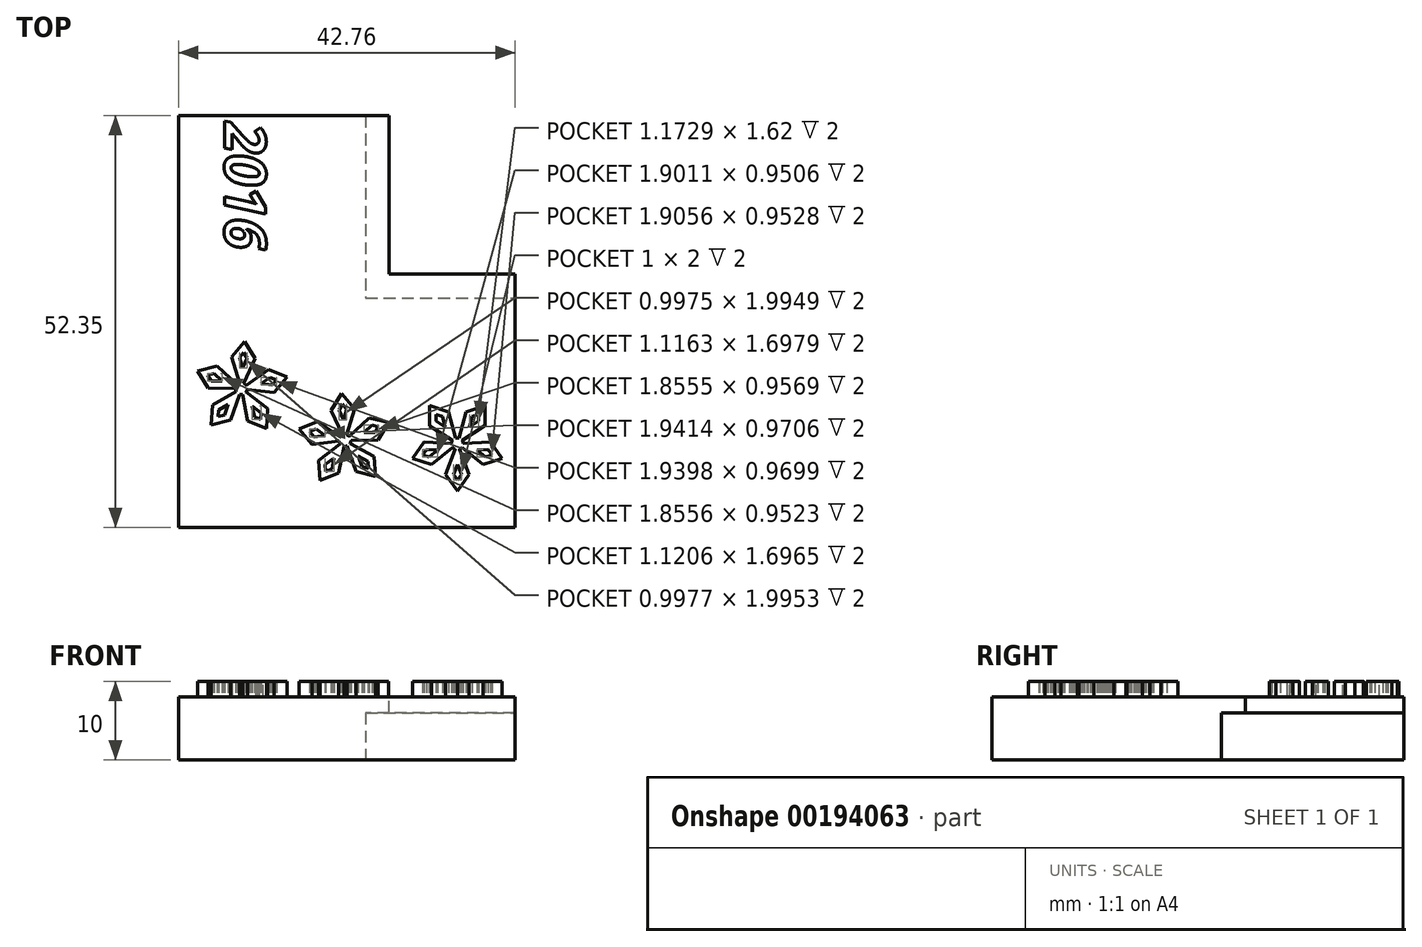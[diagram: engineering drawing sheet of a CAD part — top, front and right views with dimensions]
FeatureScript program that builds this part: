
annotation { "Feature Type Name" : "Feature", "Feature Type Description" : "" }
export const myFeature = defineFeature(function(context is Context, id is Id, definition is map)
    precondition{}
    {
        {
            var Q0;
            Q0=qCreatedBy(makeId("Top.planeOp"),FACE);
            var sketch = newSketch(context, id + "F0", { "sketchPlane" : qUnion([Q0])});
            skLineSegment(sketch, "E0.bottom", {"start": v(100, 80) * mm, "end": v(20, 80) * mm});
            skLineSegment(sketch, "E0.top", {"start": v(100, -80) * mm, "end": v(20, -80) * mm});
            skLineSegment(sketch, "E0.left", {"start": v(100, 80) * mm, "end": v(100, 20) * mm});
            skLineSegment(sketch, "E0.right", {"start": v(-100, 80) * mm, "end": v(-100, 20) * mm});
            skLineSegment(sketch, "E1.trimOffspring", {"start": v(-100, -20) * mm, "end": v(-100, -80) * mm});
            skLineSegment(sketch, "E2.trimOffspring", {"start": v(100, -20) * mm, "end": v(100, -80) * mm});
            skLineSegment(sketch, "E3.trimOffspring", {"start": v(-20, -80) * mm, "end": v(-100, -80) * mm});
            skLineSegment(sketch, "E4.trimOffspring", {"start": v(-20, 80) * mm, "end": v(-100, 80) * mm});
            skPoint(sketch, "E5.MirrorCS.end.orphan", {"position": v(100, 59.57) * mm});
            skPoint(sketch, "E5.MirrorCS.start.orphan", {"position": v(125, 0) * mm});
            skPoint(sketch, "E6.orphan", {"position": v(100, -59.57) * mm});
            skLineSegment(sketch, "E7", {"start": v(20, 80) * mm, "end": v(-20, 80) * mm});
            skLineSegment(sketch, "E8", {"start": v(100, 20) * mm, "end": v(100, -20) * mm});
            skLineSegment(sketch, "E9", {"start": v(20, -80) * mm, "end": v(-20, -80) * mm});
            skLineSegment(sketch, "E10", {"start": v(-100, -20) * mm, "end": v(-100, 20) * mm});
            skPoint(sketch, "E11.MirrorCS.end.orphan", {"position": v(0, -105) * mm});
            skPoint(sketch, "E12.start.orphan", {"position": v(0, 105) * mm});
            skPoint(sketch, "E13.MirrorCS.end.orphan", {"position": v(-125, 0) * mm});
            skSolve(sketch);
        }
        {
            var Q0;
            Q0=qSketchRegion(id+"F0",true);
            extrude(context, id + "F1", {"entities" : qUnion([Q0]), "endBound" : BoundingType.SYMMETRIC, "depth" : 8 * mm});
        }
        {
            var Q0;
            Q0=makeQuery(id+"F1.opExtrude","CAP_FACE",FACE,{"disambiguationData":[OSD([sQuery(id+"F0.wireOp",EDGE,"E0.bottom"),sQuery(id+"F0.wireOp",EDGE,"E0.top"),sQuery(id+"F0.wireOp",EDGE,"E0.left"),sQuery(id+"F0.wireOp",EDGE,"E0.right"),sQuery(id+"F0.wireOp",EDGE,"b7ca5f3b-2874-41bd-b902-1c79f96a0a8620.MirrorC"),sQuery(id+"F0.wireOp",EDGE,"b7ca5f3b-2874-41bd-b902-1c79f96a0a8621.MirrorC"),sQuery(id+"F0.wireOp",EDGE,"b7ca5f3b-2874-41bd-b902-1c79f96a0a8622.MirrorCS"),sQuery(id+"F0.wireOp",EDGE,"b7ca5f3b-2874-41bd-b902-1c79f96a0a8623.MirrorCS"),sQuery(id+"F0.wireOp",EDGE,"b7ca5f3b-2874-41bd-b902-1c79f96a0a8624.MirrorCS"),sQuery(id+"F0.wireOp",EDGE,"b7ca5f3b-2874-41bd-b902-1c79f96a0a8625.MirrorCS"),sQuery(id+"F0.wireOp",EDGE,"70034771-ba44-435e-ab74-29499f25fa1546.MirrorC"),sQuery(id+"F0.wireOp",EDGE,"70034771-ba44-435e-ab74-29499f25fa1547.MirrorCS"),sQuery(id+"F0.wireOp",EDGE,"70034771-ba44-435e-ab74-29499f25fa1548.MirrorC"),sQuery(id+"F0.wireOp",EDGE,"70034771-ba44-435e-ab74-29499f25fa1549.MirrorCS"),sQuery(id+"F0.wireOp",EDGE,"70034771-ba44-435e-ab74-29499f25fa1550.MirrorCS"),sQuery(id+"F0.wireOp",EDGE,"70034771-ba44-435e-ab74-29499f25fa1551.MirrorCS"),sQuery(id+"F0.wireOp",EDGE,"kvcqsOdL-v7G7-uprB-0sNa-MCxYedLtEpX4"),sQuery(id+"F0.wireOp",EDGE,"FiKvVNeF-WQ3T-xo78-YCTY-fOMMCtKvFc36"),sQuery(id+"F0.wireOp",EDGE,"E12"),sQuery(id+"F0.wireOp",EDGE,"E11.MirrorCS"),sQuery(id+"F0.wireOp",EDGE,"c8cf1958-df2a-43db-8a51-ccb89cce498c1.MirrorCS"),sQuery(id+"F0.wireOp",EDGE,"b5f25a3e-5a5b-413b-84b4-cc5ad052e2f90.MirrorCS"),sQuery(id+"F0.wireOp",EDGE,"E13.MirrorCS"),sQuery(id+"F0.wireOp",EDGE,"bd7b76a7-2dc2-4ffb-bbfe-847ced00b9070.MirrorCS"),sQuery(id+"F0.wireOp",EDGE,"E1.trimOffspring"),sQuery(id+"F0.wireOp",EDGE,"E2.trimOffspring"),sQuery(id+"F0.wireOp",EDGE,"E3.trimOffspring"),sQuery(id+"F0.wireOp",EDGE,"E4.trimOffspring")])],"isStart":false});
            var sketch = newSketch(context, id + "F2", { "sketchPlane" : qUnion([Q0])});
            skCircle(sketch, "E14.cCircle", {"center": v(82.22, 58.96) * mm, "radius": 6 * mm, "construction": true});
            skLineSegment(sketch, "E14.0", {"start": v(88.2, 58.66) * mm, "end": v(83.78, 53.17) * mm, "construction": true});
            skLineSegment(sketch, "E14.1", {"start": v(83.78, 53.17) * mm, "end": v(77.19, 55.68) * mm, "construction": true});
            skLineSegment(sketch, "E14.2", {"start": v(77.19, 55.68) * mm, "end": v(77.55, 62.73) * mm, "construction": true});
            skLineSegment(sketch, "E14.3", {"start": v(63.31, 55.4) * mm, "end": v(70.12, 57.24) * mm, "construction": true});
            skLineSegment(sketch, "E14.4", {"start": v(84.36, 64.57) * mm, "end": v(88.2, 58.66) * mm, "construction": true});
            skLineSegment(sketch, "E15", {"start": v(77.55, 62.73) * mm, "end": v(78.22, 60.26) * mm});
            skLineSegment(sketch, "E16", {"start": v(78.22, 60.26) * mm, "end": v(81.5, 59.2) * mm});
            skLineSegment(sketch, "E17", {"start": v(81.84, 59.6) * mm, "end": v(80.1, 62.6) * mm});
            skLineSegment(sketch, "E18", {"start": v(80.1, 62.6) * mm, "end": v(77.55, 62.73) * mm});
            skLineSegment(sketch, "E19", {"start": v(77.19, 55.68) * mm, "end": v(79.74, 55.56) * mm});
            skLineSegment(sketch, "E20", {"start": v(79.74, 55.56) * mm, "end": v(81.77, 58.35) * mm});
            skLineSegment(sketch, "E21", {"start": v(81.48, 58.8) * mm, "end": v(78.1, 58.07) * mm});
            skLineSegment(sketch, "E22", {"start": v(78.1, 58.07) * mm, "end": v(77.19, 55.68) * mm});
            skLineSegment(sketch, "E23", {"start": v(83.78, 53.17) * mm, "end": v(84.69, 55.56) * mm});
            skLineSegment(sketch, "E24", {"start": v(84.69, 55.56) * mm, "end": v(82.66, 58.35) * mm});
            skLineSegment(sketch, "E25", {"start": v(82.14, 58.21) * mm, "end": v(81.8, 54.78) * mm});
            skLineSegment(sketch, "E26", {"start": v(81.8, 54.78) * mm, "end": v(83.78, 53.17) * mm});
            skLineSegment(sketch, "E27", {"start": v(82.9, 58.66) * mm, "end": v(86.06, 57.26) * mm});
            skLineSegment(sketch, "E28", {"start": v(86.06, 57.26) * mm, "end": v(88.2, 58.66) * mm});
            skLineSegment(sketch, "E29", {"start": v(82.93, 59.2) * mm, "end": v(86.21, 60.26) * mm});
            skLineSegment(sketch, "E30", {"start": v(86.21, 60.26) * mm, "end": v(88.2, 58.66) * mm});
            skLineSegment(sketch, "E31", {"start": v(84.36, 64.57) * mm, "end": v(85.02, 62.1) * mm});
            skLineSegment(sketch, "E32", {"start": v(85.02, 62.1) * mm, "end": v(82.72, 59.52) * mm});
            skLineSegment(sketch, "E33", {"start": v(82.22, 59.71) * mm, "end": v(82.22, 63.16) * mm});
            skLineSegment(sketch, "E34", {"start": v(82.22, 63.16) * mm, "end": v(84.36, 64.57) * mm});
            skLineSegment(sketch, "E35", {"start": v(86.28, 61.61) * mm, "end": v(86, 55.91) * mm, "construction": true});
            skLineSegment(sketch, "E36", {"start": v(86, 55.91) * mm, "end": v(80.48, 54.43) * mm, "construction": true});
            skLineSegment(sketch, "E37", {"start": v(80.48, 54.43) * mm, "end": v(77.37, 59.2) * mm, "construction": true});
            skLineSegment(sketch, "E38", {"start": v(77.37, 59.2) * mm, "end": v(80.95, 63.65) * mm, "construction": true});
            skLineSegment(sketch, "E39", {"start": v(80.95, 63.65) * mm, "end": v(86.28, 61.61) * mm, "construction": true});
            skLineSegment(sketch, "E40", {"start": v(84.36, 64.57) * mm, "end": v(82.22, 58.96) * mm, "construction": true});
            skLineSegment(sketch, "E41", {"start": v(88.2, 58.66) * mm, "end": v(82.22, 58.96) * mm, "construction": true});
            skLineSegment(sketch, "E42", {"start": v(83.78, 53.17) * mm, "end": v(82.22, 58.96) * mm, "construction": true});
            skLineSegment(sketch, "E43", {"start": v(77.19, 55.68) * mm, "end": v(82.22, 58.96) * mm, "construction": true});
            skLineSegment(sketch, "E44", {"start": v(77.55, 62.73) * mm, "end": v(82.22, 58.96) * mm, "construction": true});
            skArc(sketch, "E45", {"start": v(81.77, 58.35) * mm, "mid": v(81.95, 58.26) * mm, "end": v(82.14, 58.21) * mm});
            skArc(sketch, "E46.trimOffspring", {"start": v(81.5, 59.2) * mm, "mid": v(81.47, 59) * mm, "end": v(81.48, 58.8) * mm});
            skArc(sketch, "E47.trimOffspring", {"start": v(82.22, 59.71) * mm, "mid": v(82.02, 59.69) * mm, "end": v(81.84, 59.6) * mm});
            skArc(sketch, "E48.trimOffspring", {"start": v(82.93, 59.2) * mm, "mid": v(82.84, 59.37) * mm, "end": v(82.72, 59.52) * mm});
            skArc(sketch, "E49.trimOffspring", {"start": v(82.66, 58.35) * mm, "mid": v(82.8, 58.49) * mm, "end": v(82.9, 58.66) * mm});
            skLineSegment(sketch, "E50", {"start": v(78.62, 61.86) * mm, "end": v(78.85, 61.04) * mm});
            skLineSegment(sketch, "E51", {"start": v(78.85, 61.04) * mm, "end": v(80.18, 60.6) * mm});
            skLineSegment(sketch, "E52", {"start": v(80.18, 60.6) * mm, "end": v(79.47, 61.82) * mm});
            skLineSegment(sketch, "E53", {"start": v(79.47, 61.82) * mm, "end": v(78.62, 61.86) * mm});
            skLineSegment(sketch, "E54", {"start": v(83.86, 63.28) * mm, "end": v(84.08, 62.45) * mm});
            skLineSegment(sketch, "E55", {"start": v(84.08, 62.45) * mm, "end": v(83.15, 61.4) * mm});
            skLineSegment(sketch, "E56", {"start": v(83.15, 61.4) * mm, "end": v(83.15, 62.8) * mm});
            skLineSegment(sketch, "E57", {"start": v(83.15, 62.8) * mm, "end": v(83.86, 63.28) * mm});
            skLineSegment(sketch, "E58", {"start": v(83.42, 54.5) * mm, "end": v(83.72, 55.3) * mm});
            skLineSegment(sketch, "E59", {"start": v(83.72, 55.3) * mm, "end": v(82.9, 56.43) * mm});
            skLineSegment(sketch, "E60", {"start": v(82.9, 56.43) * mm, "end": v(82.76, 55.04) * mm});
            skLineSegment(sketch, "E61", {"start": v(82.76, 55.04) * mm, "end": v(83.42, 54.5) * mm});
            skLineSegment(sketch, "E62", {"start": v(86.83, 58.73) * mm, "end": v(86.16, 59.26) * mm});
            skLineSegment(sketch, "E63", {"start": v(86.16, 59.26) * mm, "end": v(84.83, 58.83) * mm});
            skLineSegment(sketch, "E64", {"start": v(84.83, 58.83) * mm, "end": v(86.11, 58.26) * mm});
            skLineSegment(sketch, "E65", {"start": v(86.11, 58.26) * mm, "end": v(86.83, 58.73) * mm});
            skLineSegment(sketch, "E66", {"start": v(78.35, 56.44) * mm, "end": v(79.2, 56.4) * mm});
            skLineSegment(sketch, "E67", {"start": v(79.2, 56.4) * mm, "end": v(80.02, 57.53) * mm});
            skLineSegment(sketch, "E68", {"start": v(80.02, 57.53) * mm, "end": v(78.65, 57.24) * mm});
            skLineSegment(sketch, "E69", {"start": v(78.65, 57.24) * mm, "end": v(78.35, 56.44) * mm});
            skLineSegment(sketch, "E70", {"start": v(78.1, 29.78) * mm, "end": v(78.11, 27.22) * mm});
            skLineSegment(sketch, "E71", {"start": v(78.11, 27.22) * mm, "end": v(81, 25.34) * mm});
            skLineSegment(sketch, "E72", {"start": v(81.44, 25.66) * mm, "end": v(80.54, 29) * mm});
            skLineSegment(sketch, "E73", {"start": v(80.54, 29) * mm, "end": v(78.1, 29.78) * mm});
            skLineSegment(sketch, "E74", {"start": v(75.93, 23.07) * mm, "end": v(78.37, 22.29) * mm});
            skLineSegment(sketch, "E75", {"start": v(78.37, 22.29) * mm, "end": v(81.05, 24.46) * mm});
            skLineSegment(sketch, "E76", {"start": v(80.89, 24.97) * mm, "end": v(77.44, 25.14) * mm});
            skLineSegment(sketch, "E77", {"start": v(77.44, 25.14) * mm, "end": v(75.93, 23.07) * mm});
            skLineSegment(sketch, "E78", {"start": v(81.65, 18.93) * mm, "end": v(83.14, 21) * mm});
            skLineSegment(sketch, "E79", {"start": v(83.14, 21) * mm, "end": v(81.9, 24.23) * mm});
            skLineSegment(sketch, "E80", {"start": v(81.37, 24.23) * mm, "end": v(80.14, 21) * mm});
            skLineSegment(sketch, "E81", {"start": v(80.14, 21) * mm, "end": v(81.65, 18.93) * mm});
            skLineSegment(sketch, "E82", {"start": v(82.22, 24.46) * mm, "end": v(84.91, 22.3) * mm});
            skLineSegment(sketch, "E83", {"start": v(84.91, 22.3) * mm, "end": v(87.35, 23.09) * mm});
            skLineSegment(sketch, "E84", {"start": v(82.39, 24.97) * mm, "end": v(85.83, 25.15) * mm});
            skLineSegment(sketch, "E85", {"start": v(85.83, 25.15) * mm, "end": v(87.35, 23.09) * mm});
            skLineSegment(sketch, "E86", {"start": v(85.16, 29.8) * mm, "end": v(85.15, 27.24) * mm});
            skLineSegment(sketch, "E87", {"start": v(85.15, 27.24) * mm, "end": v(82.26, 25.34) * mm});
            skLineSegment(sketch, "E88", {"start": v(81.83, 25.66) * mm, "end": v(82.72, 29) * mm});
            skLineSegment(sketch, "E89", {"start": v(82.72, 29) * mm, "end": v(85.16, 29.8) * mm});
            skArc(sketch, "E90", {"start": v(81.05, 24.46) * mm, "mid": v(81.2, 24.33) * mm, "end": v(81.37, 24.23) * mm});
            skArc(sketch, "E91.trimOffspring", {"start": v(81, 25.34) * mm, "mid": v(80.92, 25.17) * mm, "end": v(80.89, 24.97) * mm});
            skArc(sketch, "E92.trimOffspring", {"start": v(81.83, 25.66) * mm, "mid": v(81.64, 25.68) * mm, "end": v(81.44, 25.66) * mm});
            skArc(sketch, "E93.trimOffspring", {"start": v(82.39, 24.97) * mm, "mid": v(82.35, 25.17) * mm, "end": v(82.26, 25.34) * mm});
            skArc(sketch, "E94.trimOffspring", {"start": v(81.9, 24.23) * mm, "mid": v(82.08, 24.33) * mm, "end": v(82.22, 24.46) * mm});
            skLineSegment(sketch, "E95", {"start": v(78.92, 28.67) * mm, "end": v(78.92, 27.81) * mm});
            skLineSegment(sketch, "E96", {"start": v(78.92, 27.81) * mm, "end": v(80.1, 27.05) * mm});
            skLineSegment(sketch, "E97", {"start": v(80.1, 27.05) * mm, "end": v(79.73, 28.4) * mm});
            skLineSegment(sketch, "E98", {"start": v(79.73, 28.4) * mm, "end": v(78.92, 28.67) * mm});
            skLineSegment(sketch, "E99", {"start": v(84.34, 28.67) * mm, "end": v(84.34, 27.82) * mm});
            skLineSegment(sketch, "E100", {"start": v(84.34, 27.82) * mm, "end": v(83.17, 27.06) * mm});
            skLineSegment(sketch, "E101", {"start": v(83.17, 27.06) * mm, "end": v(83.53, 28.4) * mm});
            skLineSegment(sketch, "E102", {"start": v(83.53, 28.4) * mm, "end": v(84.34, 28.67) * mm});
            skLineSegment(sketch, "E103", {"start": v(81.64, 20.32) * mm, "end": v(82.14, 21) * mm});
            skLineSegment(sketch, "E104", {"start": v(82.14, 21) * mm, "end": v(81.64, 22.32) * mm});
            skLineSegment(sketch, "E105", {"start": v(81.64, 22.32) * mm, "end": v(81.14, 21) * mm});
            skLineSegment(sketch, "E106", {"start": v(81.14, 21) * mm, "end": v(81.64, 20.32) * mm});
            skLineSegment(sketch, "E107", {"start": v(86.03, 23.51) * mm, "end": v(85.53, 24.2) * mm});
            skLineSegment(sketch, "E108", {"start": v(85.53, 24.2) * mm, "end": v(84.13, 24.13) * mm});
            skLineSegment(sketch, "E109", {"start": v(84.13, 24.13) * mm, "end": v(85.22, 23.25) * mm});
            skLineSegment(sketch, "E110", {"start": v(85.22, 23.25) * mm, "end": v(86.03, 23.51) * mm});
            skLineSegment(sketch, "E111", {"start": v(77.25, 23.5) * mm, "end": v(78.06, 23.24) * mm});
            skLineSegment(sketch, "E112", {"start": v(78.06, 23.24) * mm, "end": v(79.15, 24.12) * mm});
            skLineSegment(sketch, "E113", {"start": v(79.15, 24.12) * mm, "end": v(77.75, 24.19) * mm});
            skLineSegment(sketch, "E114", {"start": v(77.75, 24.19) * mm, "end": v(77.25, 23.5) * mm});
            skLineSegment(sketch, "E115", {"start": v(54.66, 73.05) * mm, "end": v(55.75, 70.73) * mm});
            skLineSegment(sketch, "E116", {"start": v(55.75, 70.73) * mm, "end": v(59.17, 70.25) * mm});
            skLineSegment(sketch, "E117", {"start": v(59.43, 70.72) * mm, "end": v(57.2, 73.36) * mm});
            skLineSegment(sketch, "E118", {"start": v(57.2, 73.36) * mm, "end": v(54.66, 73.05) * mm});
            skLineSegment(sketch, "E119", {"start": v(55.53, 66.05) * mm, "end": v(58.07, 66.37) * mm});
            skLineSegment(sketch, "E120", {"start": v(58.07, 66.37) * mm, "end": v(59.58, 69.47) * mm});
            skLineSegment(sketch, "E121", {"start": v(59.22, 69.86) * mm, "end": v(56.02, 68.56) * mm});
            skLineSegment(sketch, "E122", {"start": v(56.02, 68.56) * mm, "end": v(55.53, 66.05) * mm});
            skLineSegment(sketch, "E123", {"start": v(62.46, 64.71) * mm, "end": v(62.94, 67.23) * mm});
            skLineSegment(sketch, "E124", {"start": v(62.94, 67.23) * mm, "end": v(60.45, 69.63) * mm});
            skLineSegment(sketch, "E125", {"start": v(59.97, 69.4) * mm, "end": v(60.22, 65.95) * mm});
            skLineSegment(sketch, "E126", {"start": v(60.22, 65.95) * mm, "end": v(62.46, 64.71) * mm});
            skLineSegment(sketch, "E127", {"start": v(60.64, 69.97) * mm, "end": v(64, 69.14) * mm});
            skLineSegment(sketch, "E128", {"start": v(64, 69.14) * mm, "end": v(65.87, 70.89) * mm});
            skLineSegment(sketch, "E129", {"start": v(60.58, 70.5) * mm, "end": v(63.62, 72.12) * mm});
            skLineSegment(sketch, "E130", {"start": v(63.62, 72.12) * mm, "end": v(65.87, 70.89) * mm});
            skLineSegment(sketch, "E131", {"start": v(61.05, 76.04) * mm, "end": v(62.13, 73.72) * mm});
            skLineSegment(sketch, "E132", {"start": v(62.13, 73.72) * mm, "end": v(60.3, 70.78) * mm});
            skLineSegment(sketch, "E133", {"start": v(59.78, 70.89) * mm, "end": v(59.18, 74.29) * mm});
            skLineSegment(sketch, "E134", {"start": v(59.18, 74.29) * mm, "end": v(61.05, 76.04) * mm});
            skArc(sketch, "E135", {"start": v(59.58, 69.47) * mm, "mid": v(59.77, 69.41) * mm, "end": v(59.97, 69.4) * mm});
            skArc(sketch, "E136.trimOffspring", {"start": v(59.17, 70.25) * mm, "mid": v(59.17, 70.05) * mm, "end": v(59.22, 69.86) * mm});
            skArc(sketch, "E137.trimOffspring", {"start": v(59.78, 70.89) * mm, "mid": v(59.6, 70.83) * mm, "end": v(59.43, 70.72) * mm});
            skArc(sketch, "E138.trimOffspring", {"start": v(60.58, 70.5) * mm, "mid": v(60.46, 70.66) * mm, "end": v(60.3, 70.78) * mm});
            skArc(sketch, "E139.trimOffspring", {"start": v(60.45, 69.63) * mm, "mid": v(60.57, 69.78) * mm, "end": v(60.64, 69.97) * mm});
            skLineSegment(sketch, "E140", {"start": v(55.87, 72.38) * mm, "end": v(56.23, 71.6) * mm});
            skLineSegment(sketch, "E141", {"start": v(56.23, 71.6) * mm, "end": v(57.62, 71.41) * mm});
            skLineSegment(sketch, "E142", {"start": v(57.62, 71.41) * mm, "end": v(56.72, 72.48) * mm});
            skLineSegment(sketch, "E143", {"start": v(56.72, 72.48) * mm, "end": v(55.87, 72.38) * mm});
            skLineSegment(sketch, "E144", {"start": v(60.79, 74.68) * mm, "end": v(61.15, 73.9) * mm});
            skLineSegment(sketch, "E145", {"start": v(61.15, 73.9) * mm, "end": v(60.4, 72.72) * mm});
            skLineSegment(sketch, "E146", {"start": v(60.4, 72.72) * mm, "end": v(60.17, 74.1) * mm});
            skLineSegment(sketch, "E147", {"start": v(60.17, 74.1) * mm, "end": v(60.79, 74.68) * mm});
            skLineSegment(sketch, "E148", {"start": v(61.87, 65.96) * mm, "end": v(62.03, 66.8) * mm});
            skLineSegment(sketch, "E149", {"start": v(62.03, 66.8) * mm, "end": v(61.02, 67.78) * mm});
            skLineSegment(sketch, "E150", {"start": v(61.02, 67.78) * mm, "end": v(61.13, 66.38) * mm});
            skLineSegment(sketch, "E151", {"start": v(61.13, 66.38) * mm, "end": v(61.87, 65.96) * mm});
            skLineSegment(sketch, "E152", {"start": v(64.5, 70.72) * mm, "end": v(63.75, 71.13) * mm});
            skLineSegment(sketch, "E153", {"start": v(63.75, 71.13) * mm, "end": v(62.5, 70.47) * mm});
            skLineSegment(sketch, "E154", {"start": v(62.5, 70.47) * mm, "end": v(63.87, 70.13) * mm});
            skLineSegment(sketch, "E155", {"start": v(63.87, 70.13) * mm, "end": v(64.5, 70.72) * mm});
            skLineSegment(sketch, "E156", {"start": v(56.54, 67) * mm, "end": v(57.39, 67.1) * mm});
            skLineSegment(sketch, "E157", {"start": v(57.39, 67.1) * mm, "end": v(58, 68.36) * mm});
            skLineSegment(sketch, "E158", {"start": v(58, 68.36) * mm, "end": v(56.7, 67.83) * mm});
            skLineSegment(sketch, "E159", {"start": v(56.7, 67.83) * mm, "end": v(56.54, 67) * mm});
            skLineSegment(sketch, "E160", {"start": v(86.68, 11.24) * mm, "end": v(87.35, 8.78) * mm});
            skLineSegment(sketch, "E161", {"start": v(87.35, 8.78) * mm, "end": v(90.64, 7.7) * mm});
            skLineSegment(sketch, "E162", {"start": v(90.97, 8.12) * mm, "end": v(89.24, 11.1) * mm});
            skLineSegment(sketch, "E163", {"start": v(89.24, 11.1) * mm, "end": v(86.68, 11.24) * mm});
            skLineSegment(sketch, "E164", {"start": v(86.32, 4.2) * mm, "end": v(88.88, 4.08) * mm});
            skLineSegment(sketch, "E165", {"start": v(88.88, 4.08) * mm, "end": v(90.91, 6.87) * mm});
            skLineSegment(sketch, "E166", {"start": v(90.62, 7.32) * mm, "end": v(87.24, 6.59) * mm});
            skLineSegment(sketch, "E167", {"start": v(87.24, 6.59) * mm, "end": v(86.32, 4.2) * mm});
            skLineSegment(sketch, "E168", {"start": v(92.91, 1.68) * mm, "end": v(93.82, 4.08) * mm});
            skLineSegment(sketch, "E169", {"start": v(93.82, 4.08) * mm, "end": v(91.8, 6.87) * mm});
            skLineSegment(sketch, "E170", {"start": v(91.27, 6.73) * mm, "end": v(90.93, 3.3) * mm});
            skLineSegment(sketch, "E171", {"start": v(90.93, 3.3) * mm, "end": v(92.91, 1.68) * mm});
            skLineSegment(sketch, "E172", {"start": v(92.04, 7.17) * mm, "end": v(95.2, 5.78) * mm});
            skLineSegment(sketch, "E173", {"start": v(95.2, 5.78) * mm, "end": v(97.34, 7.17) * mm});
            skLineSegment(sketch, "E174", {"start": v(92.06, 7.7) * mm, "end": v(95.35, 8.78) * mm});
            skLineSegment(sketch, "E175", {"start": v(95.35, 8.78) * mm, "end": v(97.34, 7.17) * mm});
            skLineSegment(sketch, "E176", {"start": v(93.5, 13.08) * mm, "end": v(94.15, 10.6) * mm});
            skLineSegment(sketch, "E177", {"start": v(94.15, 10.6) * mm, "end": v(91.85, 8.04) * mm});
            skLineSegment(sketch, "E178", {"start": v(91.35, 8.23) * mm, "end": v(91.35, 11.68) * mm});
            skLineSegment(sketch, "E179", {"start": v(91.35, 11.68) * mm, "end": v(93.5, 13.08) * mm});
            skArc(sketch, "E180", {"start": v(90.91, 6.87) * mm, "mid": v(91.08, 6.78) * mm, "end": v(91.27, 6.73) * mm});
            skArc(sketch, "E181.trimOffspring", {"start": v(90.64, 7.7) * mm, "mid": v(90.6, 7.51) * mm, "end": v(90.62, 7.32) * mm});
            skArc(sketch, "E182.trimOffspring", {"start": v(91.35, 8.23) * mm, "mid": v(91.16, 8.2) * mm, "end": v(90.97, 8.12) * mm});
            skArc(sketch, "E183.trimOffspring", {"start": v(92.06, 7.7) * mm, "mid": v(91.98, 7.89) * mm, "end": v(91.85, 8.04) * mm});
            skArc(sketch, "E184.trimOffspring", {"start": v(91.8, 6.87) * mm, "mid": v(91.93, 7) * mm, "end": v(92.04, 7.17) * mm});
            skLineSegment(sketch, "E185", {"start": v(87.76, 10.38) * mm, "end": v(87.98, 9.55) * mm});
            skLineSegment(sketch, "E186", {"start": v(87.98, 9.55) * mm, "end": v(89.31, 9.12) * mm});
            skLineSegment(sketch, "E187", {"start": v(89.31, 9.12) * mm, "end": v(88.6, 10.33) * mm});
            skLineSegment(sketch, "E188", {"start": v(88.6, 10.33) * mm, "end": v(87.76, 10.38) * mm});
            skLineSegment(sketch, "E189", {"start": v(93, 11.8) * mm, "end": v(93.22, 10.97) * mm});
            skLineSegment(sketch, "E190", {"start": v(93.22, 10.97) * mm, "end": v(92.29, 9.92) * mm});
            skLineSegment(sketch, "E191", {"start": v(92.29, 9.92) * mm, "end": v(92.29, 11.32) * mm});
            skLineSegment(sketch, "E192", {"start": v(92.29, 11.32) * mm, "end": v(93, 11.8) * mm});
            skLineSegment(sketch, "E193", {"start": v(92.55, 3.02) * mm, "end": v(92.86, 3.81) * mm});
            skLineSegment(sketch, "E194", {"start": v(92.86, 3.81) * mm, "end": v(92.03, 4.95) * mm});
            skLineSegment(sketch, "E195", {"start": v(92.03, 4.95) * mm, "end": v(91.9, 3.55) * mm});
            skLineSegment(sketch, "E196", {"start": v(91.9, 3.55) * mm, "end": v(92.55, 3.02) * mm});
            skLineSegment(sketch, "E197", {"start": v(95.96, 7.24) * mm, "end": v(95.3, 7.78) * mm});
            skLineSegment(sketch, "E198", {"start": v(95.3, 7.78) * mm, "end": v(93.96, 7.34) * mm});
            skLineSegment(sketch, "E199", {"start": v(93.96, 7.34) * mm, "end": v(95.25, 6.78) * mm});
            skLineSegment(sketch, "E200", {"start": v(95.25, 6.78) * mm, "end": v(95.96, 7.24) * mm});
            skLineSegment(sketch, "E201", {"start": v(87.48, 4.95) * mm, "end": v(88.33, 4.91) * mm});
            skLineSegment(sketch, "E202", {"start": v(88.33, 4.91) * mm, "end": v(89.16, 6.05) * mm});
            skLineSegment(sketch, "E203", {"start": v(89.16, 6.05) * mm, "end": v(87.79, 5.75) * mm});
            skLineSegment(sketch, "E204", {"start": v(87.79, 5.75) * mm, "end": v(87.48, 4.95) * mm});
            skLineSegment(sketch, "E205", {"start": v(76.28, -11.06) * mm, "end": v(77.37, -13.38) * mm});
            skLineSegment(sketch, "E206", {"start": v(77.37, -13.38) * mm, "end": v(80.8, -13.86) * mm});
            skLineSegment(sketch, "E207", {"start": v(81.05, -13.4) * mm, "end": v(78.82, -10.75) * mm});
            skLineSegment(sketch, "E208", {"start": v(78.82, -10.75) * mm, "end": v(76.28, -11.06) * mm});
            skLineSegment(sketch, "E209", {"start": v(77.15, -18.06) * mm, "end": v(79.7, -17.74) * mm});
            skLineSegment(sketch, "E210", {"start": v(79.7, -17.74) * mm, "end": v(81.2, -14.64) * mm});
            skLineSegment(sketch, "E211", {"start": v(80.84, -14.25) * mm, "end": v(77.64, -15.55) * mm});
            skLineSegment(sketch, "E212", {"start": v(77.64, -15.55) * mm, "end": v(77.15, -18.06) * mm});
            skLineSegment(sketch, "E213", {"start": v(84.08, -19.4) * mm, "end": v(84.56, -16.88) * mm});
            skLineSegment(sketch, "E214", {"start": v(84.56, -16.88) * mm, "end": v(82.08, -14.49) * mm});
            skLineSegment(sketch, "E215", {"start": v(81.6, -14.71) * mm, "end": v(81.84, -18.16) * mm});
            skLineSegment(sketch, "E216", {"start": v(81.84, -18.16) * mm, "end": v(84.08, -19.4) * mm});
            skLineSegment(sketch, "E217", {"start": v(82.26, -14.14) * mm, "end": v(85.62, -14.97) * mm});
            skLineSegment(sketch, "E218", {"start": v(85.62, -14.97) * mm, "end": v(87.49, -13.22) * mm});
            skLineSegment(sketch, "E219", {"start": v(82.2, -13.61) * mm, "end": v(85.25, -12) * mm});
            skLineSegment(sketch, "E220", {"start": v(85.25, -12) * mm, "end": v(87.49, -13.22) * mm});
            skLineSegment(sketch, "E221", {"start": v(82.67, -8.07) * mm, "end": v(83.75, -10.4) * mm});
            skLineSegment(sketch, "E222", {"start": v(83.75, -10.4) * mm, "end": v(81.93, -13.33) * mm});
            skLineSegment(sketch, "E223", {"start": v(81.4, -13.23) * mm, "end": v(80.8, -9.82) * mm});
            skLineSegment(sketch, "E224", {"start": v(80.8, -9.82) * mm, "end": v(82.67, -8.07) * mm});
            skArc(sketch, "E225", {"start": v(81.2, -14.64) * mm, "mid": v(81.4, -14.7) * mm, "end": v(81.6, -14.71) * mm});
            skArc(sketch, "E226.trimOffspring", {"start": v(80.8, -13.86) * mm, "mid": v(80.8, -14.06) * mm, "end": v(80.84, -14.25) * mm});
            skArc(sketch, "E227.trimOffspring", {"start": v(81.4, -13.23) * mm, "mid": v(81.22, -13.29) * mm, "end": v(81.05, -13.4) * mm});
            skArc(sketch, "E228.trimOffspring", {"start": v(82.2, -13.61) * mm, "mid": v(82.08, -13.45) * mm, "end": v(81.93, -13.33) * mm});
            skArc(sketch, "E229.trimOffspring", {"start": v(82.08, -14.49) * mm, "mid": v(82.2, -14.33) * mm, "end": v(82.26, -14.14) * mm});
            skLineSegment(sketch, "E230", {"start": v(77.5, -11.73) * mm, "end": v(77.86, -12.5) * mm});
            skLineSegment(sketch, "E231", {"start": v(77.86, -12.5) * mm, "end": v(79.24, -12.7) * mm});
            skLineSegment(sketch, "E232", {"start": v(79.24, -12.7) * mm, "end": v(78.34, -11.63) * mm});
            skLineSegment(sketch, "E233", {"start": v(78.34, -11.63) * mm, "end": v(77.5, -11.73) * mm});
            skLineSegment(sketch, "E234", {"start": v(82.4, -9.43) * mm, "end": v(82.77, -10.2) * mm});
            skLineSegment(sketch, "E235", {"start": v(82.77, -10.2) * mm, "end": v(82.03, -11.4) * mm});
            skLineSegment(sketch, "E236", {"start": v(82.03, -11.4) * mm, "end": v(81.79, -10.01) * mm});
            skLineSegment(sketch, "E237", {"start": v(81.79, -10.01) * mm, "end": v(82.4, -9.43) * mm});
            skLineSegment(sketch, "E238", {"start": v(83.5, -18.15) * mm, "end": v(83.65, -17.3) * mm});
            skLineSegment(sketch, "E239", {"start": v(83.65, -17.3) * mm, "end": v(82.65, -16.34) * mm});
            skLineSegment(sketch, "E240", {"start": v(82.65, -16.34) * mm, "end": v(82.75, -17.73) * mm});
            skLineSegment(sketch, "E241", {"start": v(82.75, -17.73) * mm, "end": v(83.5, -18.15) * mm});
            skLineSegment(sketch, "E242", {"start": v(86.12, -13.4) * mm, "end": v(85.37, -12.98) * mm});
            skLineSegment(sketch, "E243", {"start": v(85.37, -12.98) * mm, "end": v(84.13, -13.64) * mm});
            skLineSegment(sketch, "E244", {"start": v(84.13, -13.64) * mm, "end": v(85.5, -13.98) * mm});
            skLineSegment(sketch, "E245", {"start": v(85.5, -13.98) * mm, "end": v(86.12, -13.4) * mm});
            skLineSegment(sketch, "E246", {"start": v(78.16, -17.12) * mm, "end": v(79, -17.01) * mm});
            skLineSegment(sketch, "E247", {"start": v(79, -17.01) * mm, "end": v(79.62, -15.75) * mm});
            skLineSegment(sketch, "E248", {"start": v(79.62, -15.75) * mm, "end": v(78.33, -16.28) * mm});
            skLineSegment(sketch, "E249", {"start": v(78.33, -16.28) * mm, "end": v(78.16, -17.12) * mm});
            skLineSegment(sketch, "E250", {"start": v(62.15, -63.73) * mm, "end": v(63.24, -66.04) * mm});
            skLineSegment(sketch, "E251", {"start": v(63.24, -66.04) * mm, "end": v(66.66, -66.52) * mm});
            skLineSegment(sketch, "E252", {"start": v(66.92, -66.05) * mm, "end": v(64.7, -63.42) * mm});
            skLineSegment(sketch, "E253", {"start": v(64.7, -63.42) * mm, "end": v(62.15, -63.73) * mm});
            skLineSegment(sketch, "E254", {"start": v(63.02, -70.73) * mm, "end": v(65.56, -70.4) * mm});
            skLineSegment(sketch, "E255", {"start": v(65.56, -70.4) * mm, "end": v(67.08, -67.3) * mm});
            skLineSegment(sketch, "E256", {"start": v(66.71, -66.91) * mm, "end": v(63.51, -68.22) * mm});
            skLineSegment(sketch, "E257", {"start": v(63.51, -68.22) * mm, "end": v(63.02, -70.73) * mm});
            skLineSegment(sketch, "E258", {"start": v(69.95, -72.06) * mm, "end": v(70.43, -69.55) * mm});
            skLineSegment(sketch, "E259", {"start": v(70.43, -69.55) * mm, "end": v(67.94, -67.15) * mm});
            skLineSegment(sketch, "E260", {"start": v(67.46, -67.38) * mm, "end": v(67.71, -70.82) * mm});
            skLineSegment(sketch, "E261", {"start": v(67.71, -70.82) * mm, "end": v(69.95, -72.06) * mm});
            skLineSegment(sketch, "E262", {"start": v(68.13, -66.8) * mm, "end": v(71.49, -67.63) * mm});
            skLineSegment(sketch, "E263", {"start": v(71.49, -67.63) * mm, "end": v(73.36, -65.89) * mm});
            skLineSegment(sketch, "E264", {"start": v(68.07, -66.28) * mm, "end": v(71.12, -64.65) * mm});
            skLineSegment(sketch, "E265", {"start": v(71.12, -64.65) * mm, "end": v(73.36, -65.89) * mm});
            skLineSegment(sketch, "E266", {"start": v(68.54, -60.74) * mm, "end": v(69.62, -63.06) * mm});
            skLineSegment(sketch, "E267", {"start": v(69.62, -63.06) * mm, "end": v(67.8, -66) * mm});
            skLineSegment(sketch, "E268", {"start": v(67.27, -65.89) * mm, "end": v(66.68, -62.49) * mm});
            skLineSegment(sketch, "E269", {"start": v(66.68, -62.49) * mm, "end": v(68.54, -60.74) * mm});
            skArc(sketch, "E270", {"start": v(67.08, -67.3) * mm, "mid": v(67.26, -67.36) * mm, "end": v(67.46, -67.38) * mm});
            skArc(sketch, "E271.trimOffspring", {"start": v(66.66, -66.52) * mm, "mid": v(66.66, -66.72) * mm, "end": v(66.71, -66.91) * mm});
            skArc(sketch, "E272.trimOffspring", {"start": v(67.27, -65.89) * mm, "mid": v(67.09, -65.95) * mm, "end": v(66.92, -66.05) * mm});
            skArc(sketch, "E273.trimOffspring", {"start": v(68.07, -66.28) * mm, "mid": v(67.95, -66.12) * mm, "end": v(67.8, -66) * mm});
            skArc(sketch, "E274.trimOffspring", {"start": v(67.94, -67.15) * mm, "mid": v(68.06, -67) * mm, "end": v(68.13, -66.8) * mm});
            skLineSegment(sketch, "E275", {"start": v(63.36, -64.4) * mm, "end": v(63.73, -65.17) * mm});
            skLineSegment(sketch, "E276", {"start": v(63.73, -65.17) * mm, "end": v(65.11, -65.36) * mm});
            skLineSegment(sketch, "E277", {"start": v(65.11, -65.36) * mm, "end": v(64.2, -64.3) * mm});
            skLineSegment(sketch, "E278", {"start": v(64.2, -64.3) * mm, "end": v(63.36, -64.4) * mm});
            skLineSegment(sketch, "E279", {"start": v(68.28, -62.1) * mm, "end": v(68.64, -62.87) * mm});
            skLineSegment(sketch, "E280", {"start": v(68.64, -62.87) * mm, "end": v(67.9, -64.06) * mm});
            skLineSegment(sketch, "E281", {"start": v(67.9, -64.06) * mm, "end": v(67.66, -62.68) * mm});
            skLineSegment(sketch, "E282", {"start": v(67.66, -62.68) * mm, "end": v(68.28, -62.1) * mm});
            skLineSegment(sketch, "E283", {"start": v(69.36, -70.8) * mm, "end": v(69.52, -69.97) * mm});
            skLineSegment(sketch, "E284", {"start": v(69.52, -69.97) * mm, "end": v(68.52, -69) * mm});
            skLineSegment(sketch, "E285", {"start": v(68.52, -69) * mm, "end": v(68.62, -70.4) * mm});
            skLineSegment(sketch, "E286", {"start": v(68.62, -70.4) * mm, "end": v(69.36, -70.8) * mm});
            skLineSegment(sketch, "E287", {"start": v(71.99, -66.06) * mm, "end": v(71.24, -65.65) * mm});
            skLineSegment(sketch, "E288", {"start": v(71.24, -65.65) * mm, "end": v(70, -66.3) * mm});
            skLineSegment(sketch, "E289", {"start": v(70, -66.3) * mm, "end": v(71.36, -66.64) * mm});
            skLineSegment(sketch, "E290", {"start": v(71.36, -66.64) * mm, "end": v(71.99, -66.06) * mm});
            skLineSegment(sketch, "E291", {"start": v(64.03, -69.78) * mm, "end": v(64.88, -69.68) * mm});
            skLineSegment(sketch, "E292", {"start": v(64.88, -69.68) * mm, "end": v(65.5, -68.42) * mm});
            skLineSegment(sketch, "E293", {"start": v(65.5, -68.42) * mm, "end": v(64.2, -68.95) * mm});
            skLineSegment(sketch, "E294", {"start": v(64.2, -68.95) * mm, "end": v(64.03, -69.78) * mm});
            skLineSegment(sketch, "E295", {"start": v(31.31, 68.24) * mm, "end": v(33.35, 66.7) * mm});
            skLineSegment(sketch, "E296", {"start": v(33.35, 66.7) * mm, "end": v(36.6, 67.86) * mm});
            skLineSegment(sketch, "E297", {"start": v(36.62, 68.4) * mm, "end": v(33.42, 69.7) * mm});
            skLineSegment(sketch, "E298", {"start": v(33.42, 69.7) * mm, "end": v(31.31, 68.24) * mm});
            skLineSegment(sketch, "E299", {"start": v(35.33, 62.45) * mm, "end": v(37.43, 63.9) * mm});
            skLineSegment(sketch, "E300", {"start": v(37.43, 63.9) * mm, "end": v(37.33, 67.36) * mm});
            skLineSegment(sketch, "E301", {"start": v(36.83, 67.54) * mm, "end": v(34.6, 64.9) * mm});
            skLineSegment(sketch, "E302", {"start": v(34.6, 64.9) * mm, "end": v(35.33, 62.45) * mm});
            skLineSegment(sketch, "E303", {"start": v(42.09, 64.48) * mm, "end": v(41.34, 66.93) * mm});
            skLineSegment(sketch, "E304", {"start": v(41.34, 66.93) * mm, "end": v(38.03, 67.9) * mm});
            skLineSegment(sketch, "E305", {"start": v(37.7, 67.47) * mm, "end": v(39.53, 64.54) * mm});
            skLineSegment(sketch, "E306", {"start": v(39.53, 64.54) * mm, "end": v(42.09, 64.48) * mm});
            skLineSegment(sketch, "E307", {"start": v(38.04, 68.29) * mm, "end": v(41.4, 69.11) * mm});
            skLineSegment(sketch, "E308", {"start": v(41.4, 69.11) * mm, "end": v(42.24, 71.53) * mm});
            skLineSegment(sketch, "E309", {"start": v(37.73, 68.73) * mm, "end": v(39.68, 71.58) * mm});
            skLineSegment(sketch, "E310", {"start": v(39.68, 71.58) * mm, "end": v(42.24, 71.53) * mm});
            skLineSegment(sketch, "E311", {"start": v(35.58, 73.86) * mm, "end": v(37.62, 72.3) * mm});
            skLineSegment(sketch, "E312", {"start": v(37.62, 72.3) * mm, "end": v(37.37, 68.86) * mm});
            skLineSegment(sketch, "E313", {"start": v(36.85, 68.7) * mm, "end": v(34.74, 71.44) * mm});
            skLineSegment(sketch, "E314", {"start": v(34.74, 71.44) * mm, "end": v(35.58, 73.86) * mm});
            skArc(sketch, "E315", {"start": v(37.33, 67.36) * mm, "mid": v(37.53, 67.4) * mm, "end": v(37.7, 67.47) * mm});
            skArc(sketch, "E316.trimOffspring", {"start": v(36.6, 67.86) * mm, "mid": v(36.7, 67.68) * mm, "end": v(36.83, 67.54) * mm});
            skArc(sketch, "E317.trimOffspring", {"start": v(36.85, 68.7) * mm, "mid": v(36.71, 68.56) * mm, "end": v(36.62, 68.4) * mm});
            skArc(sketch, "E318.trimOffspring", {"start": v(37.73, 68.73) * mm, "mid": v(37.56, 68.82) * mm, "end": v(37.37, 68.86) * mm});
            skArc(sketch, "E319.trimOffspring", {"start": v(38.03, 67.9) * mm, "mid": v(38.06, 68.1) * mm, "end": v(38.04, 68.29) * mm});
            skLineSegment(sketch, "E320", {"start": v(32.7, 68.21) * mm, "end": v(33.37, 67.7) * mm});
            skLineSegment(sketch, "E321", {"start": v(33.37, 67.7) * mm, "end": v(34.7, 68.17) * mm});
            skLineSegment(sketch, "E322", {"start": v(34.7, 68.17) * mm, "end": v(33.4, 68.7) * mm});
            skLineSegment(sketch, "E323", {"start": v(33.4, 68.7) * mm, "end": v(32.7, 68.21) * mm});
            skLineSegment(sketch, "E324", {"start": v(35.98, 72.53) * mm, "end": v(36.66, 72.01) * mm});
            skLineSegment(sketch, "E325", {"start": v(36.66, 72.01) * mm, "end": v(36.56, 70.62) * mm});
            skLineSegment(sketch, "E326", {"start": v(36.56, 70.62) * mm, "end": v(35.7, 71.73) * mm});
            skLineSegment(sketch, "E327", {"start": v(35.7, 71.73) * mm, "end": v(35.98, 72.53) * mm});
            skLineSegment(sketch, "E328", {"start": v(40.99, 65.31) * mm, "end": v(40.74, 66.13) * mm});
            skLineSegment(sketch, "E329", {"start": v(40.74, 66.13) * mm, "end": v(39.4, 66.52) * mm});
            skLineSegment(sketch, "E330", {"start": v(39.4, 66.52) * mm, "end": v(40.13, 65.33) * mm});
            skLineSegment(sketch, "E331", {"start": v(40.13, 65.33) * mm, "end": v(40.99, 65.31) * mm});
            skLineSegment(sketch, "E332", {"start": v(41.1, 70.74) * mm, "end": v(40.25, 70.76) * mm});
            skLineSegment(sketch, "E333", {"start": v(40.25, 70.76) * mm, "end": v(39.46, 69.6) * mm});
            skLineSegment(sketch, "E334", {"start": v(39.46, 69.6) * mm, "end": v(40.82, 69.94) * mm});
            skLineSegment(sketch, "E335", {"start": v(40.82, 69.94) * mm, "end": v(41.1, 70.74) * mm});
            skLineSegment(sketch, "E336", {"start": v(35.79, 63.75) * mm, "end": v(36.49, 64.24) * mm});
            skLineSegment(sketch, "E337", {"start": v(36.49, 64.24) * mm, "end": v(36.45, 65.64) * mm});
            skLineSegment(sketch, "E338", {"start": v(36.45, 65.64) * mm, "end": v(35.54, 64.57) * mm});
            skLineSegment(sketch, "E339", {"start": v(35.54, 64.57) * mm, "end": v(35.79, 63.75) * mm});
            skLineSegment(sketch, "E340", {"start": v(-1.67, 69.03) * mm, "end": v(-1, 66.56) * mm});
            skLineSegment(sketch, "E341", {"start": v(-1, 66.56) * mm, "end": v(2.28, 65.49) * mm});
            skLineSegment(sketch, "E342", {"start": v(2.62, 65.9) * mm, "end": v(0.88, 68.9) * mm});
            skLineSegment(sketch, "E343", {"start": v(0.88, 68.9) * mm, "end": v(-1.67, 69.03) * mm});
            skLineSegment(sketch, "E344", {"start": v(-2.03, 61.98) * mm, "end": v(0.52, 61.86) * mm});
            skLineSegment(sketch, "E345", {"start": v(0.52, 61.86) * mm, "end": v(2.55, 64.65) * mm});
            skLineSegment(sketch, "E346", {"start": v(2.26, 65.1) * mm, "end": v(-1.11, 64.37) * mm});
            skLineSegment(sketch, "E347", {"start": v(-1.11, 64.37) * mm, "end": v(-2.03, 61.98) * mm});
            skLineSegment(sketch, "E348", {"start": v(4.56, 59.46) * mm, "end": v(5.47, 61.86) * mm});
            skLineSegment(sketch, "E349", {"start": v(5.47, 61.86) * mm, "end": v(3.44, 64.65) * mm});
            skLineSegment(sketch, "E350", {"start": v(2.92, 64.51) * mm, "end": v(2.57, 61.08) * mm});
            skLineSegment(sketch, "E351", {"start": v(2.57, 61.08) * mm, "end": v(4.56, 59.46) * mm});
            skLineSegment(sketch, "E352", {"start": v(3.68, 64.95) * mm, "end": v(6.84, 63.56) * mm});
            skLineSegment(sketch, "E353", {"start": v(6.84, 63.56) * mm, "end": v(8.99, 64.95) * mm});
            skLineSegment(sketch, "E354", {"start": v(3.7, 65.49) * mm, "end": v(7, 66.56) * mm});
            skLineSegment(sketch, "E355", {"start": v(7, 66.56) * mm, "end": v(8.99, 64.95) * mm});
            skLineSegment(sketch, "E356", {"start": v(5.14, 70.86) * mm, "end": v(5.8, 68.4) * mm});
            skLineSegment(sketch, "E357", {"start": v(5.8, 68.4) * mm, "end": v(3.5, 65.82) * mm});
            skLineSegment(sketch, "E358", {"start": v(3, 66) * mm, "end": v(3, 69.46) * mm});
            skLineSegment(sketch, "E359", {"start": v(3, 69.46) * mm, "end": v(5.14, 70.86) * mm});
            skArc(sketch, "E360", {"start": v(2.55, 64.65) * mm, "mid": v(2.73, 64.56) * mm, "end": v(2.92, 64.51) * mm});
            skArc(sketch, "E361.trimOffspring", {"start": v(2.28, 65.49) * mm, "mid": v(2.25, 65.3) * mm, "end": v(2.26, 65.1) * mm});
            skArc(sketch, "E362.trimOffspring", {"start": v(3, 66) * mm, "mid": v(2.8, 65.98) * mm, "end": v(2.62, 65.9) * mm});
            skArc(sketch, "E363.trimOffspring", {"start": v(3.7, 65.49) * mm, "mid": v(3.62, 65.67) * mm, "end": v(3.5, 65.82) * mm});
            skArc(sketch, "E364.trimOffspring", {"start": v(3.44, 64.65) * mm, "mid": v(3.58, 64.79) * mm, "end": v(3.68, 64.95) * mm});
            skLineSegment(sketch, "E365", {"start": v(-0.6, 68.16) * mm, "end": v(-0.37, 67.33) * mm});
            skLineSegment(sketch, "E366", {"start": v(-0.37, 67.33) * mm, "end": v(0.96, 66.9) * mm});
            skLineSegment(sketch, "E367", {"start": v(0.96, 66.9) * mm, "end": v(0.25, 68.11) * mm});
            skLineSegment(sketch, "E368", {"start": v(0.25, 68.11) * mm, "end": v(-0.6, 68.16) * mm});
            skLineSegment(sketch, "E369", {"start": v(4.64, 69.57) * mm, "end": v(4.86, 68.75) * mm});
            skLineSegment(sketch, "E370", {"start": v(4.86, 68.75) * mm, "end": v(3.93, 67.7) * mm});
            skLineSegment(sketch, "E371", {"start": v(3.93, 67.7) * mm, "end": v(3.93, 69.1) * mm});
            skLineSegment(sketch, "E372", {"start": v(3.93, 69.1) * mm, "end": v(4.64, 69.57) * mm});
            skLineSegment(sketch, "E373", {"start": v(4.2, 60.8) * mm, "end": v(4.5, 61.6) * mm});
            skLineSegment(sketch, "E374", {"start": v(4.5, 61.6) * mm, "end": v(3.68, 62.73) * mm});
            skLineSegment(sketch, "E375", {"start": v(3.68, 62.73) * mm, "end": v(3.54, 61.34) * mm});
            skLineSegment(sketch, "E376", {"start": v(3.54, 61.34) * mm, "end": v(4.2, 60.8) * mm});
            skLineSegment(sketch, "E377", {"start": v(7.6, 65.02) * mm, "end": v(6.94, 65.56) * mm});
            skLineSegment(sketch, "E378", {"start": v(6.94, 65.56) * mm, "end": v(5.6, 65.13) * mm});
            skLineSegment(sketch, "E379", {"start": v(5.6, 65.13) * mm, "end": v(6.9, 64.56) * mm});
            skLineSegment(sketch, "E380", {"start": v(6.9, 64.56) * mm, "end": v(7.6, 65.02) * mm});
            skLineSegment(sketch, "E381", {"start": v(-0.87, 62.74) * mm, "end": v(-0.02, 62.7) * mm});
            skLineSegment(sketch, "E382", {"start": v(-0.02, 62.7) * mm, "end": v(0.8, 63.83) * mm});
            skLineSegment(sketch, "E383", {"start": v(0.8, 63.83) * mm, "end": v(-0.57, 63.53) * mm});
            skLineSegment(sketch, "E384", {"start": v(-0.57, 63.53) * mm, "end": v(-0.87, 62.74) * mm});
            skLineSegment(sketch, "E385", {"start": v(11.6, 69.26) * mm, "end": v(13.97, 68.28) * mm});
            skLineSegment(sketch, "E386", {"start": v(13.97, 68.28) * mm, "end": v(16.82, 70.22) * mm});
            skLineSegment(sketch, "E387", {"start": v(16.7, 70.74) * mm, "end": v(13.28, 71.2) * mm});
            skLineSegment(sketch, "E388", {"start": v(13.28, 71.2) * mm, "end": v(11.6, 69.26) * mm});
            skLineSegment(sketch, "E389", {"start": v(16.96, 64.66) * mm, "end": v(18.62, 66.6) * mm});
            skLineSegment(sketch, "E390", {"start": v(18.62, 66.6) * mm, "end": v(17.65, 69.92) * mm});
            skLineSegment(sketch, "E391", {"start": v(17.12, 69.97) * mm, "end": v(15.63, 66.85) * mm});
            skLineSegment(sketch, "E392", {"start": v(15.63, 66.85) * mm, "end": v(16.96, 64.66) * mm});
            skLineSegment(sketch, "E393", {"start": v(22.98, 68.33) * mm, "end": v(21.65, 70.51) * mm});
            skLineSegment(sketch, "E394", {"start": v(21.65, 70.51) * mm, "end": v(18.2, 70.62) * mm});
            skLineSegment(sketch, "E395", {"start": v(17.99, 70.13) * mm, "end": v(20.49, 67.75) * mm});
            skLineSegment(sketch, "E396", {"start": v(20.49, 67.75) * mm, "end": v(22.98, 68.33) * mm});
            skLineSegment(sketch, "E397", {"start": v(18.1, 71) * mm, "end": v(21.14, 72.64) * mm});
            skLineSegment(sketch, "E398", {"start": v(21.14, 72.64) * mm, "end": v(21.35, 75.2) * mm});
            skLineSegment(sketch, "E399", {"start": v(17.7, 71.35) * mm, "end": v(18.87, 74.6) * mm});
            skLineSegment(sketch, "E400", {"start": v(18.87, 74.6) * mm, "end": v(21.35, 75.2) * mm});
            skLineSegment(sketch, "E401", {"start": v(14.32, 75.77) * mm, "end": v(16.68, 74.78) * mm});
            skLineSegment(sketch, "E402", {"start": v(16.68, 74.78) * mm, "end": v(17.3, 71.38) * mm});
            skLineSegment(sketch, "E403", {"start": v(16.85, 71.1) * mm, "end": v(14.12, 73.22) * mm});
            skLineSegment(sketch, "E404", {"start": v(14.12, 73.22) * mm, "end": v(14.32, 75.77) * mm});
            skArc(sketch, "E405", {"start": v(17.65, 69.92) * mm, "mid": v(17.83, 70) * mm, "end": v(17.99, 70.13) * mm});
            skArc(sketch, "E406.trimOffspring", {"start": v(16.82, 70.22) * mm, "mid": v(16.96, 70.07) * mm, "end": v(17.12, 69.97) * mm});
            skArc(sketch, "E407.trimOffspring", {"start": v(16.85, 71.1) * mm, "mid": v(16.75, 70.93) * mm, "end": v(16.7, 70.74) * mm});
            skArc(sketch, "E408.trimOffspring", {"start": v(17.7, 71.35) * mm, "mid": v(17.5, 71.4) * mm, "end": v(17.3, 71.38) * mm});
            skArc(sketch, "E409.trimOffspring", {"start": v(18.2, 70.62) * mm, "mid": v(18.17, 70.82) * mm, "end": v(18.1, 71) * mm});
            skLineSegment(sketch, "E410", {"start": v(12.95, 69.58) * mm, "end": v(13.74, 69.25) * mm});
            skLineSegment(sketch, "E411", {"start": v(13.74, 69.25) * mm, "end": v(14.9, 70.04) * mm});
            skLineSegment(sketch, "E412", {"start": v(14.9, 70.04) * mm, "end": v(13.5, 70.22) * mm});
            skLineSegment(sketch, "E413", {"start": v(13.5, 70.22) * mm, "end": v(12.95, 69.58) * mm});
            skLineSegment(sketch, "E414", {"start": v(15.04, 74.59) * mm, "end": v(15.83, 74.26) * mm});
            skLineSegment(sketch, "E415", {"start": v(15.83, 74.26) * mm, "end": v(16.08, 72.88) * mm});
            skLineSegment(sketch, "E416", {"start": v(16.08, 72.88) * mm, "end": v(14.97, 73.74) * mm});
            skLineSegment(sketch, "E417", {"start": v(14.97, 73.74) * mm, "end": v(15.04, 74.59) * mm});
            skLineSegment(sketch, "E418", {"start": v(21.7, 68.86) * mm, "end": v(21.26, 69.6) * mm});
            skLineSegment(sketch, "E419", {"start": v(21.26, 69.6) * mm, "end": v(19.86, 69.63) * mm});
            skLineSegment(sketch, "E420", {"start": v(19.86, 69.63) * mm, "end": v(20.88, 68.67) * mm});
            skLineSegment(sketch, "E421", {"start": v(20.88, 68.67) * mm, "end": v(21.7, 68.86) * mm});
            skLineSegment(sketch, "E422", {"start": v(20.45, 74.15) * mm, "end": v(19.62, 73.95) * mm});
            skLineSegment(sketch, "E423", {"start": v(19.62, 73.95) * mm, "end": v(19.15, 72.63) * mm});
            skLineSegment(sketch, "E424", {"start": v(19.15, 72.63) * mm, "end": v(20.38, 73.3) * mm});
            skLineSegment(sketch, "E425", {"start": v(20.38, 73.3) * mm, "end": v(20.45, 74.15) * mm});
            skLineSegment(sketch, "E426", {"start": v(17.07, 66.04) * mm, "end": v(17.62, 66.69) * mm});
            skLineSegment(sketch, "E427", {"start": v(17.62, 66.69) * mm, "end": v(17.23, 68.03) * mm});
            skLineSegment(sketch, "E428", {"start": v(17.23, 68.03) * mm, "end": v(16.63, 66.77) * mm});
            skLineSegment(sketch, "E429", {"start": v(16.63, 66.77) * mm, "end": v(17.07, 66.04) * mm});
            skLineSegment(sketch, "E430", {"start": v(22.28, -68.24) * mm, "end": v(23.75, -70.33) * mm});
            skLineSegment(sketch, "E431", {"start": v(23.75, -70.33) * mm, "end": v(27.2, -70.21) * mm});
            skLineSegment(sketch, "E432", {"start": v(27.38, -69.7) * mm, "end": v(24.72, -67.5) * mm});
            skLineSegment(sketch, "E433", {"start": v(24.72, -67.5) * mm, "end": v(22.28, -68.24) * mm});
            skLineSegment(sketch, "E434", {"start": v(24.35, -74.98) * mm, "end": v(26.8, -74.23) * mm});
            skLineSegment(sketch, "E435", {"start": v(26.8, -74.23) * mm, "end": v(27.75, -70.9) * mm});
            skLineSegment(sketch, "E436", {"start": v(27.32, -70.58) * mm, "end": v(24.4, -72.42) * mm});
            skLineSegment(sketch, "E437", {"start": v(24.4, -72.42) * mm, "end": v(24.35, -74.98) * mm});
            skLineSegment(sketch, "E438", {"start": v(31.4, -75.1) * mm, "end": v(31.44, -72.53) * mm});
            skLineSegment(sketch, "E439", {"start": v(31.44, -72.53) * mm, "end": v(28.58, -70.6) * mm});
            skLineSegment(sketch, "E440", {"start": v(28.14, -70.91) * mm, "end": v(28.98, -74.26) * mm});
            skLineSegment(sketch, "E441", {"start": v(28.98, -74.26) * mm, "end": v(31.4, -75.1) * mm});
            skLineSegment(sketch, "E442", {"start": v(28.7, -70.23) * mm, "end": v(32.15, -70.46) * mm});
            skLineSegment(sketch, "E443", {"start": v(32.15, -70.46) * mm, "end": v(33.69, -68.42) * mm});
            skLineSegment(sketch, "E444", {"start": v(28.54, -69.72) * mm, "end": v(31.27, -67.6) * mm});
            skLineSegment(sketch, "E445", {"start": v(31.27, -67.6) * mm, "end": v(33.69, -68.42) * mm});
            skLineSegment(sketch, "E446", {"start": v(28.05, -64.18) * mm, "end": v(29.52, -66.28) * mm});
            skLineSegment(sketch, "E447", {"start": v(29.52, -66.28) * mm, "end": v(28.23, -69.49) * mm});
            skLineSegment(sketch, "E448", {"start": v(27.7, -69.48) * mm, "end": v(26.52, -66.23) * mm});
            skLineSegment(sketch, "E449", {"start": v(26.52, -66.23) * mm, "end": v(28.05, -64.18) * mm});
            skArc(sketch, "E450", {"start": v(27.75, -70.9) * mm, "mid": v(27.94, -70.93) * mm, "end": v(28.14, -70.91) * mm});
            skArc(sketch, "E451.trimOffspring", {"start": v(27.2, -70.21) * mm, "mid": v(27.24, -70.4) * mm, "end": v(27.32, -70.58) * mm});
            skArc(sketch, "E452.trimOffspring", {"start": v(27.7, -69.48) * mm, "mid": v(27.52, -69.57) * mm, "end": v(27.38, -69.7) * mm});
            skArc(sketch, "E453.trimOffspring", {"start": v(28.54, -69.72) * mm, "mid": v(28.4, -69.58) * mm, "end": v(28.23, -69.49) * mm});
            skArc(sketch, "E454.trimOffspring", {"start": v(28.58, -70.6) * mm, "mid": v(28.66, -70.43) * mm, "end": v(28.7, -70.23) * mm});
            skLineSegment(sketch, "E455", {"start": v(23.59, -68.69) * mm, "end": v(24.08, -69.38) * mm});
            skLineSegment(sketch, "E456", {"start": v(24.08, -69.38) * mm, "end": v(25.48, -69.34) * mm});
            skLineSegment(sketch, "E457", {"start": v(25.48, -69.34) * mm, "end": v(24.4, -68.44) * mm});
            skLineSegment(sketch, "E458", {"start": v(24.4, -68.44) * mm, "end": v(23.59, -68.69) * mm});
            skLineSegment(sketch, "E459", {"start": v(28.03, -65.57) * mm, "end": v(28.52, -66.27) * mm});
            skLineSegment(sketch, "E460", {"start": v(28.52, -66.27) * mm, "end": v(28, -67.57) * mm});
            skLineSegment(sketch, "E461", {"start": v(28, -67.57) * mm, "end": v(27.52, -66.25) * mm});
            skLineSegment(sketch, "E462", {"start": v(27.52, -66.25) * mm, "end": v(28.03, -65.57) * mm});
            skLineSegment(sketch, "E463", {"start": v(30.6, -73.96) * mm, "end": v(30.62, -73.1) * mm});
            skLineSegment(sketch, "E464", {"start": v(30.62, -73.1) * mm, "end": v(29.46, -72.33) * mm});
            skLineSegment(sketch, "E465", {"start": v(29.46, -72.33) * mm, "end": v(29.8, -73.68) * mm});
            skLineSegment(sketch, "E466", {"start": v(29.8, -73.68) * mm, "end": v(30.6, -73.96) * mm});
            skLineSegment(sketch, "E467", {"start": v(32.37, -68.83) * mm, "end": v(31.56, -68.55) * mm});
            skLineSegment(sketch, "E468", {"start": v(31.56, -68.55) * mm, "end": v(30.45, -69.42) * mm});
            skLineSegment(sketch, "E469", {"start": v(30.45, -69.42) * mm, "end": v(31.85, -69.5) * mm});
            skLineSegment(sketch, "E470", {"start": v(31.85, -69.5) * mm, "end": v(32.37, -68.83) * mm});
            skLineSegment(sketch, "E471", {"start": v(25.18, -73.88) * mm, "end": v(26, -73.62) * mm});
            skLineSegment(sketch, "E472", {"start": v(26, -73.62) * mm, "end": v(26.38, -72.28) * mm});
            skLineSegment(sketch, "E473", {"start": v(26.38, -72.28) * mm, "end": v(25.2, -73.02) * mm});
            skLineSegment(sketch, "E474", {"start": v(25.2, -73.02) * mm, "end": v(25.18, -73.88) * mm});
            skLineSegment(sketch, "E475", {"start": v(-16.22, 74.04) * mm, "end": v(-16.65, 71.52) * mm});
            skLineSegment(sketch, "E476", {"start": v(-16.65, 71.52) * mm, "end": v(-14.13, 69.16) * mm});
            skLineSegment(sketch, "E477", {"start": v(-13.65, 69.4) * mm, "end": v(-13.96, 72.84) * mm});
            skLineSegment(sketch, "E478", {"start": v(-13.96, 72.84) * mm, "end": v(-16.22, 74.04) * mm});
            skLineSegment(sketch, "E479", {"start": v(-19.52, 67.8) * mm, "end": v(-17.26, 66.61) * mm});
            skLineSegment(sketch, "E480", {"start": v(-17.26, 66.61) * mm, "end": v(-14.23, 68.29) * mm});
            skLineSegment(sketch, "E481", {"start": v(-14.31, 68.82) * mm, "end": v(-17.68, 69.58) * mm});
            skLineSegment(sketch, "E482", {"start": v(-17.68, 69.58) * mm, "end": v(-19.52, 67.8) * mm});
            skLineSegment(sketch, "E483", {"start": v(-14.61, 62.74) * mm, "end": v(-12.78, 64.52) * mm});
            skLineSegment(sketch, "E484", {"start": v(-12.78, 64.52) * mm, "end": v(-13.44, 67.91) * mm});
            skLineSegment(sketch, "E485", {"start": v(-13.96, 68) * mm, "end": v(-15.73, 65.04) * mm});
            skLineSegment(sketch, "E486", {"start": v(-15.73, 65.04) * mm, "end": v(-14.61, 62.74) * mm});
            skLineSegment(sketch, "E487", {"start": v(-13.08, 68.09) * mm, "end": v(-10.81, 65.49) * mm});
            skLineSegment(sketch, "E488", {"start": v(-10.81, 65.49) * mm, "end": v(-8.28, 65.84) * mm});
            skLineSegment(sketch, "E489", {"start": v(-12.83, 68.56) * mm, "end": v(-9.4, 68.14) * mm});
            skLineSegment(sketch, "E490", {"start": v(-9.4, 68.14) * mm, "end": v(-8.28, 65.84) * mm});
            skLineSegment(sketch, "E491", {"start": v(-9.27, 72.82) * mm, "end": v(-9.71, 70.3) * mm});
            skLineSegment(sketch, "E492", {"start": v(-9.71, 70.3) * mm, "end": v(-12.89, 68.95) * mm});
            skLineSegment(sketch, "E493", {"start": v(-13.26, 69.33) * mm, "end": v(-11.8, 72.46) * mm});
            skLineSegment(sketch, "E494", {"start": v(-11.8, 72.46) * mm, "end": v(-9.27, 72.82) * mm});
            skArc(sketch, "E495", {"start": v(-14.23, 68.29) * mm, "mid": v(-14.12, 68.13) * mm, "end": v(-13.96, 68) * mm});
            skArc(sketch, "E496.trimOffspring", {"start": v(-14.13, 69.16) * mm, "mid": v(-14.24, 69) * mm, "end": v(-14.31, 68.82) * mm});
            skArc(sketch, "E497.trimOffspring", {"start": v(-13.26, 69.33) * mm, "mid": v(-13.45, 69.39) * mm, "end": v(-13.65, 69.4) * mm});
            skArc(sketch, "E498.trimOffspring", {"start": v(-12.83, 68.56) * mm, "mid": v(-12.84, 68.76) * mm, "end": v(-12.89, 68.95) * mm});
            skArc(sketch, "E499.trimOffspring", {"start": v(-13.44, 67.91) * mm, "mid": v(-13.25, 67.98) * mm, "end": v(-13.08, 68.09) * mm});
            skLineSegment(sketch, "E500", {"start": v(-15.61, 72.8) * mm, "end": v(-15.76, 71.96) * mm});
            skLineSegment(sketch, "E501", {"start": v(-15.76, 71.96) * mm, "end": v(-14.73, 71) * mm});
            skLineSegment(sketch, "E502", {"start": v(-14.73, 71) * mm, "end": v(-14.86, 72.4) * mm});
            skLineSegment(sketch, "E503", {"start": v(-14.86, 72.4) * mm, "end": v(-15.61, 72.8) * mm});
            skLineSegment(sketch, "E504", {"start": v(-10.26, 71.86) * mm, "end": v(-10.41, 71.02) * mm});
            skLineSegment(sketch, "E505", {"start": v(-10.41, 71.02) * mm, "end": v(-11.7, 70.47) * mm});
            skLineSegment(sketch, "E506", {"start": v(-11.7, 70.47) * mm, "end": v(-11.1, 71.74) * mm});
            skLineSegment(sketch, "E507", {"start": v(-11.1, 71.74) * mm, "end": v(-10.26, 71.86) * mm});
            skLineSegment(sketch, "E508", {"start": v(-14.37, 64.1) * mm, "end": v(-13.76, 64.7) * mm});
            skLineSegment(sketch, "E509", {"start": v(-13.76, 64.7) * mm, "end": v(-14.03, 66.07) * mm});
            skLineSegment(sketch, "E510", {"start": v(-14.03, 66.07) * mm, "end": v(-14.75, 64.87) * mm});
            skLineSegment(sketch, "E511", {"start": v(-14.75, 64.87) * mm, "end": v(-14.37, 64.1) * mm});
            skLineSegment(sketch, "E512", {"start": v(-9.5, 66.49) * mm, "end": v(-9.87, 67.25) * mm});
            skLineSegment(sketch, "E513", {"start": v(-9.87, 67.25) * mm, "end": v(-11.27, 67.43) * mm});
            skLineSegment(sketch, "E514", {"start": v(-11.27, 67.43) * mm, "end": v(-10.34, 66.37) * mm});
            skLineSegment(sketch, "E515", {"start": v(-10.34, 66.37) * mm, "end": v(-9.5, 66.49) * mm});
            skLineSegment(sketch, "E516", {"start": v(-18.15, 68) * mm, "end": v(-17.4, 67.6) * mm});
            skLineSegment(sketch, "E517", {"start": v(-17.4, 67.6) * mm, "end": v(-16.17, 68.28) * mm});
            skLineSegment(sketch, "E518", {"start": v(-16.17, 68.28) * mm, "end": v(-17.54, 68.6) * mm});
            skLineSegment(sketch, "E519", {"start": v(-17.54, 68.6) * mm, "end": v(-18.15, 68) * mm});
            skLineSegment(sketch, "E520", {"start": v(-14.28, -69.49) * mm, "end": v(-12.99, -71.7) * mm});
            skLineSegment(sketch, "E521", {"start": v(-12.99, -71.7) * mm, "end": v(-9.54, -71.88) * mm});
            skLineSegment(sketch, "E522", {"start": v(-9.32, -71.39) * mm, "end": v(-11.77, -68.95) * mm});
            skLineSegment(sketch, "E523", {"start": v(-11.77, -68.95) * mm, "end": v(-14.28, -69.49) * mm});
            skLineSegment(sketch, "E524", {"start": v(-12.8, -76.38) * mm, "end": v(-10.3, -75.84) * mm});
            skLineSegment(sketch, "E525", {"start": v(-10.3, -75.84) * mm, "end": v(-9.06, -72.62) * mm});
            skLineSegment(sketch, "E526", {"start": v(-9.46, -72.26) * mm, "end": v(-12.53, -73.84) * mm});
            skLineSegment(sketch, "E527", {"start": v(-12.53, -73.84) * mm, "end": v(-12.8, -76.38) * mm});
            skLineSegment(sketch, "E528", {"start": v(-5.78, -77.1) * mm, "end": v(-5.52, -74.56) * mm});
            skLineSegment(sketch, "E529", {"start": v(-5.52, -74.56) * mm, "end": v(-8.2, -72.39) * mm});
            skLineSegment(sketch, "E530", {"start": v(-8.67, -72.66) * mm, "end": v(-8.12, -76.07) * mm});
            skLineSegment(sketch, "E531", {"start": v(-8.12, -76.07) * mm, "end": v(-5.78, -77.1) * mm});
            skLineSegment(sketch, "E532", {"start": v(-8.05, -72.03) * mm, "end": v(-4.64, -72.56) * mm});
            skLineSegment(sketch, "E533", {"start": v(-4.64, -72.56) * mm, "end": v(-2.92, -70.66) * mm});
            skLineSegment(sketch, "E534", {"start": v(-8.16, -71.5) * mm, "end": v(-5.27, -69.63) * mm});
            skLineSegment(sketch, "E535", {"start": v(-5.27, -69.63) * mm, "end": v(-2.92, -70.66) * mm});
            skLineSegment(sketch, "E536", {"start": v(-8.17, -65.95) * mm, "end": v(-6.9, -68.16) * mm});
            skLineSegment(sketch, "E537", {"start": v(-6.9, -68.16) * mm, "end": v(-8.45, -71.25) * mm});
            skLineSegment(sketch, "E538", {"start": v(-8.99, -71.2) * mm, "end": v(-9.88, -67.86) * mm});
            skLineSegment(sketch, "E539", {"start": v(-9.88, -67.86) * mm, "end": v(-8.17, -65.95) * mm});
            skArc(sketch, "E540", {"start": v(-9.06, -72.62) * mm, "mid": v(-8.87, -72.66) * mm, "end": v(-8.67, -72.66) * mm});
            skArc(sketch, "E541.trimOffspring", {"start": v(-9.54, -71.88) * mm, "mid": v(-9.52, -72.07) * mm, "end": v(-9.46, -72.26) * mm});
            skArc(sketch, "E542.trimOffspring", {"start": v(-8.99, -71.2) * mm, "mid": v(-9.17, -71.27) * mm, "end": v(-9.32, -71.39) * mm});
            skArc(sketch, "E543.trimOffspring", {"start": v(-8.16, -71.5) * mm, "mid": v(-8.3, -71.36) * mm, "end": v(-8.45, -71.25) * mm});
            skArc(sketch, "E544.trimOffspring", {"start": v(-8.2, -72.39) * mm, "mid": v(-8.1, -72.22) * mm, "end": v(-8.05, -72.03) * mm});
            skLineSegment(sketch, "E545", {"start": v(-13.01, -70.05) * mm, "end": v(-12.58, -70.78) * mm});
            skLineSegment(sketch, "E546", {"start": v(-12.58, -70.78) * mm, "end": v(-11.18, -70.86) * mm});
            skLineSegment(sketch, "E547", {"start": v(-11.18, -70.86) * mm, "end": v(-12.18, -69.87) * mm});
            skLineSegment(sketch, "E548", {"start": v(-12.18, -69.87) * mm, "end": v(-13.01, -70.05) * mm});
            skLineSegment(sketch, "E549", {"start": v(-8.32, -67.32) * mm, "end": v(-7.89, -68.06) * mm});
            skLineSegment(sketch, "E550", {"start": v(-7.89, -68.06) * mm, "end": v(-8.52, -69.31) * mm});
            skLineSegment(sketch, "E551", {"start": v(-8.52, -69.31) * mm, "end": v(-8.88, -67.96) * mm});
            skLineSegment(sketch, "E552", {"start": v(-8.88, -67.96) * mm, "end": v(-8.32, -67.32) * mm});
            skLineSegment(sketch, "E553", {"start": v(-6.48, -75.91) * mm, "end": v(-6.39, -75.06) * mm});
            skLineSegment(sketch, "E554", {"start": v(-6.39, -75.06) * mm, "end": v(-7.48, -74.18) * mm});
            skLineSegment(sketch, "E555", {"start": v(-7.48, -74.18) * mm, "end": v(-7.25, -75.56) * mm});
            skLineSegment(sketch, "E556", {"start": v(-7.25, -75.56) * mm, "end": v(-6.48, -75.91) * mm});
            skLineSegment(sketch, "E557", {"start": v(-4.27, -70.95) * mm, "end": v(-5.06, -70.6) * mm});
            skLineSegment(sketch, "E558", {"start": v(-5.06, -70.6) * mm, "end": v(-6.23, -71.37) * mm});
            skLineSegment(sketch, "E559", {"start": v(-6.23, -71.37) * mm, "end": v(-4.85, -71.58) * mm});
            skLineSegment(sketch, "E560", {"start": v(-4.85, -71.58) * mm, "end": v(-4.27, -70.95) * mm});
            skLineSegment(sketch, "E561", {"start": v(-11.88, -75.35) * mm, "end": v(-11.04, -75.17) * mm});
            skLineSegment(sketch, "E562", {"start": v(-11.04, -75.17) * mm, "end": v(-10.54, -73.86) * mm});
            skLineSegment(sketch, "E563", {"start": v(-10.54, -73.86) * mm, "end": v(-11.79, -74.5) * mm});
            skLineSegment(sketch, "E564", {"start": v(-11.79, -74.5) * mm, "end": v(-11.88, -75.35) * mm});
            skLineSegment(sketch, "E565", {"start": v(-49.38, 72.68) * mm, "end": v(-49.37, 70.12) * mm});
            skLineSegment(sketch, "E566", {"start": v(-49.37, 70.12) * mm, "end": v(-46.48, 68.24) * mm});
            skLineSegment(sketch, "E567", {"start": v(-46.05, 68.55) * mm, "end": v(-46.95, 71.89) * mm});
            skLineSegment(sketch, "E568", {"start": v(-46.95, 71.89) * mm, "end": v(-49.38, 72.68) * mm});
            skLineSegment(sketch, "E569", {"start": v(-51.55, 65.97) * mm, "end": v(-49.12, 65.18) * mm});
            skLineSegment(sketch, "E570", {"start": v(-49.12, 65.18) * mm, "end": v(-46.43, 67.36) * mm});
            skLineSegment(sketch, "E571", {"start": v(-46.6, 67.87) * mm, "end": v(-50.05, 68.04) * mm});
            skLineSegment(sketch, "E572", {"start": v(-50.05, 68.04) * mm, "end": v(-51.55, 65.97) * mm});
            skLineSegment(sketch, "E573", {"start": v(-45.84, 61.83) * mm, "end": v(-44.34, 63.9) * mm});
            skLineSegment(sketch, "E574", {"start": v(-44.34, 63.9) * mm, "end": v(-45.58, 67.13) * mm});
            skLineSegment(sketch, "E575", {"start": v(-46.12, 67.13) * mm, "end": v(-47.34, 63.9) * mm});
            skLineSegment(sketch, "E576", {"start": v(-47.34, 63.9) * mm, "end": v(-45.84, 61.83) * mm});
            skLineSegment(sketch, "E577", {"start": v(-45.26, 67.36) * mm, "end": v(-42.57, 65.2) * mm});
            skLineSegment(sketch, "E578", {"start": v(-42.57, 65.2) * mm, "end": v(-40.14, 65.98) * mm});
            skLineSegment(sketch, "E579", {"start": v(-45.1, 67.87) * mm, "end": v(-41.65, 68.05) * mm});
            skLineSegment(sketch, "E580", {"start": v(-41.65, 68.05) * mm, "end": v(-40.14, 65.98) * mm});
            skLineSegment(sketch, "E581", {"start": v(-42.33, 72.69) * mm, "end": v(-42.33, 70.13) * mm});
            skLineSegment(sketch, "E582", {"start": v(-42.33, 70.13) * mm, "end": v(-45.22, 68.24) * mm});
            skLineSegment(sketch, "E583", {"start": v(-45.65, 68.55) * mm, "end": v(-44.76, 71.9) * mm});
            skLineSegment(sketch, "E584", {"start": v(-44.76, 71.9) * mm, "end": v(-42.33, 72.69) * mm});
            skArc(sketch, "E585", {"start": v(-46.43, 67.36) * mm, "mid": v(-46.29, 67.22) * mm, "end": v(-46.12, 67.13) * mm});
            skArc(sketch, "E586.trimOffspring", {"start": v(-46.48, 68.24) * mm, "mid": v(-46.56, 68.06) * mm, "end": v(-46.6, 67.87) * mm});
            skArc(sketch, "E587.trimOffspring", {"start": v(-45.65, 68.55) * mm, "mid": v(-45.85, 68.58) * mm, "end": v(-46.05, 68.55) * mm});
            skArc(sketch, "E588.trimOffspring", {"start": v(-45.1, 67.87) * mm, "mid": v(-45.14, 68.06) * mm, "end": v(-45.22, 68.24) * mm});
            skArc(sketch, "E589.trimOffspring", {"start": v(-45.58, 67.13) * mm, "mid": v(-45.4, 67.22) * mm, "end": v(-45.26, 67.36) * mm});
            skLineSegment(sketch, "E590", {"start": v(-48.57, 71.56) * mm, "end": v(-48.57, 70.7) * mm});
            skLineSegment(sketch, "E591", {"start": v(-48.57, 70.7) * mm, "end": v(-47.4, 69.95) * mm});
            skLineSegment(sketch, "E592", {"start": v(-47.4, 69.95) * mm, "end": v(-47.76, 71.3) * mm});
            skLineSegment(sketch, "E593", {"start": v(-47.76, 71.3) * mm, "end": v(-48.57, 71.56) * mm});
            skLineSegment(sketch, "E594", {"start": v(-43.14, 71.57) * mm, "end": v(-43.14, 70.72) * mm});
            skLineSegment(sketch, "E595", {"start": v(-43.14, 70.72) * mm, "end": v(-44.31, 69.95) * mm});
            skLineSegment(sketch, "E596", {"start": v(-44.31, 69.95) * mm, "end": v(-43.95, 71.3) * mm});
            skLineSegment(sketch, "E597", {"start": v(-43.95, 71.3) * mm, "end": v(-43.14, 71.57) * mm});
            skLineSegment(sketch, "E598", {"start": v(-45.84, 63.21) * mm, "end": v(-45.34, 63.9) * mm});
            skLineSegment(sketch, "E599", {"start": v(-45.34, 63.9) * mm, "end": v(-45.84, 65.21) * mm});
            skLineSegment(sketch, "E600", {"start": v(-45.84, 65.21) * mm, "end": v(-46.34, 63.9) * mm});
            skLineSegment(sketch, "E601", {"start": v(-46.34, 63.9) * mm, "end": v(-45.84, 63.21) * mm});
            skLineSegment(sketch, "E602", {"start": v(-41.45, 66.4) * mm, "end": v(-41.96, 67.1) * mm});
            skLineSegment(sketch, "E603", {"start": v(-41.96, 67.1) * mm, "end": v(-43.36, 67.03) * mm});
            skLineSegment(sketch, "E604", {"start": v(-43.36, 67.03) * mm, "end": v(-42.27, 66.15) * mm});
            skLineSegment(sketch, "E605", {"start": v(-42.27, 66.15) * mm, "end": v(-41.45, 66.4) * mm});
            skLineSegment(sketch, "E606", {"start": v(-50.24, 66.4) * mm, "end": v(-49.43, 66.13) * mm});
            skLineSegment(sketch, "E607", {"start": v(-49.43, 66.13) * mm, "end": v(-48.34, 67.02) * mm});
            skLineSegment(sketch, "E608", {"start": v(-48.34, 67.02) * mm, "end": v(-49.74, 67.09) * mm});
            skLineSegment(sketch, "E609", {"start": v(-49.74, 67.09) * mm, "end": v(-50.24, 66.4) * mm});
            skLineSegment(sketch, "E610", {"start": v(-60.64, 76.38) * mm, "end": v(-62.96, 75.3) * mm});
            skLineSegment(sketch, "E611", {"start": v(-62.96, 75.3) * mm, "end": v(-63.44, 71.87) * mm});
            skLineSegment(sketch, "E612", {"start": v(-62.97, 71.61) * mm, "end": v(-60.33, 73.84) * mm});
            skLineSegment(sketch, "E613", {"start": v(-60.33, 73.84) * mm, "end": v(-60.64, 76.38) * mm});
            skLineSegment(sketch, "E614", {"start": v(-67.64, 75.51) * mm, "end": v(-67.32, 72.97) * mm});
            skLineSegment(sketch, "E615", {"start": v(-67.32, 72.97) * mm, "end": v(-64.22, 71.46) * mm});
            skLineSegment(sketch, "E616", {"start": v(-63.83, 71.82) * mm, "end": v(-65.13, 75.02) * mm});
            skLineSegment(sketch, "E617", {"start": v(-65.13, 75.02) * mm, "end": v(-67.64, 75.51) * mm});
            skLineSegment(sketch, "E618", {"start": v(-68.98, 68.59) * mm, "end": v(-66.46, 68.1) * mm});
            skLineSegment(sketch, "E619", {"start": v(-66.46, 68.1) * mm, "end": v(-64.06, 70.6) * mm});
            skLineSegment(sketch, "E620", {"start": v(-64.3, 71.08) * mm, "end": v(-67.74, 70.82) * mm});
            skLineSegment(sketch, "E621", {"start": v(-67.74, 70.82) * mm, "end": v(-68.98, 68.59) * mm});
            skLineSegment(sketch, "E622", {"start": v(-63.72, 70.4) * mm, "end": v(-64.55, 67.05) * mm});
            skLineSegment(sketch, "E623", {"start": v(-64.55, 67.05) * mm, "end": v(-62.8, 65.18) * mm});
            skLineSegment(sketch, "E624", {"start": v(-63.2, 70.47) * mm, "end": v(-61.57, 67.42) * mm});
            skLineSegment(sketch, "E625", {"start": v(-61.57, 67.42) * mm, "end": v(-62.8, 65.18) * mm});
            skLineSegment(sketch, "E626", {"start": v(-57.65, 70) * mm, "end": v(-59.97, 68.91) * mm});
            skLineSegment(sketch, "E627", {"start": v(-59.97, 68.91) * mm, "end": v(-62.9, 70.73) * mm});
            skLineSegment(sketch, "E628", {"start": v(-62.8, 71.26) * mm, "end": v(-59.4, 71.86) * mm});
            skLineSegment(sketch, "E629", {"start": v(-59.4, 71.86) * mm, "end": v(-57.65, 70) * mm});
            skArc(sketch, "E630", {"start": v(-64.22, 71.46) * mm, "mid": v(-64.28, 71.27) * mm, "end": v(-64.3, 71.08) * mm});
            skArc(sketch, "E631.trimOffspring", {"start": v(-63.44, 71.87) * mm, "mid": v(-63.64, 71.87) * mm, "end": v(-63.83, 71.82) * mm});
            skArc(sketch, "E632.trimOffspring", {"start": v(-62.8, 71.26) * mm, "mid": v(-62.86, 71.45) * mm, "end": v(-62.97, 71.61) * mm});
            skArc(sketch, "E633.trimOffspring", {"start": v(-63.2, 70.47) * mm, "mid": v(-63.03, 70.58) * mm, "end": v(-62.9, 70.73) * mm});
            skArc(sketch, "E634.trimOffspring", {"start": v(-64.06, 70.6) * mm, "mid": v(-63.9, 70.47) * mm, "end": v(-63.72, 70.4) * mm});
            skLineSegment(sketch, "E635", {"start": v(-61.31, 75.17) * mm, "end": v(-62.08, 74.8) * mm});
            skLineSegment(sketch, "E636", {"start": v(-62.08, 74.8) * mm, "end": v(-62.28, 73.42) * mm});
            skLineSegment(sketch, "E637", {"start": v(-62.28, 73.42) * mm, "end": v(-61.2, 74.33) * mm});
            skLineSegment(sketch, "E638", {"start": v(-61.2, 74.33) * mm, "end": v(-61.31, 75.17) * mm});
            skLineSegment(sketch, "E639", {"start": v(-59, 70.26) * mm, "end": v(-59.78, 69.9) * mm});
            skLineSegment(sketch, "E640", {"start": v(-59.78, 69.9) * mm, "end": v(-60.97, 70.63) * mm});
            skLineSegment(sketch, "E641", {"start": v(-60.97, 70.63) * mm, "end": v(-59.6, 70.88) * mm});
            skLineSegment(sketch, "E642", {"start": v(-59.6, 70.88) * mm, "end": v(-59, 70.26) * mm});
            skLineSegment(sketch, "E643", {"start": v(-67.73, 69.17) * mm, "end": v(-66.89, 69.01) * mm});
            skLineSegment(sketch, "E644", {"start": v(-66.89, 69.01) * mm, "end": v(-65.91, 70.02) * mm});
            skLineSegment(sketch, "E645", {"start": v(-65.91, 70.02) * mm, "end": v(-67.31, 69.92) * mm});
            skLineSegment(sketch, "E646", {"start": v(-67.31, 69.92) * mm, "end": v(-67.73, 69.17) * mm});
            skLineSegment(sketch, "E647", {"start": v(-62.97, 66.55) * mm, "end": v(-62.56, 67.3) * mm});
            skLineSegment(sketch, "E648", {"start": v(-62.56, 67.3) * mm, "end": v(-63.22, 68.53) * mm});
            skLineSegment(sketch, "E649", {"start": v(-63.22, 68.53) * mm, "end": v(-63.55, 67.17) * mm});
            skLineSegment(sketch, "E650", {"start": v(-63.55, 67.17) * mm, "end": v(-62.97, 66.55) * mm});
            skLineSegment(sketch, "E651", {"start": v(-66.7, 74.5) * mm, "end": v(-66.6, 73.66) * mm});
            skLineSegment(sketch, "E652", {"start": v(-66.6, 73.66) * mm, "end": v(-65.33, 73.04) * mm});
            skLineSegment(sketch, "E653", {"start": v(-65.33, 73.04) * mm, "end": v(-65.86, 74.34) * mm});
            skLineSegment(sketch, "E654", {"start": v(-65.86, 74.34) * mm, "end": v(-66.7, 74.5) * mm});
            skLineSegment(sketch, "E655", {"start": v(-34.14, 75.39) * mm, "end": v(-33.47, 72.92) * mm});
            skLineSegment(sketch, "E656", {"start": v(-33.47, 72.92) * mm, "end": v(-30.19, 71.85) * mm});
            skLineSegment(sketch, "E657", {"start": v(-29.85, 72.27) * mm, "end": v(-31.59, 75.25) * mm});
            skLineSegment(sketch, "E658", {"start": v(-31.59, 75.25) * mm, "end": v(-34.14, 75.39) * mm});
            skLineSegment(sketch, "E659", {"start": v(-34.5, 68.34) * mm, "end": v(-31.95, 68.22) * mm});
            skLineSegment(sketch, "E660", {"start": v(-31.95, 68.22) * mm, "end": v(-29.92, 71.01) * mm});
            skLineSegment(sketch, "E661", {"start": v(-30.2, 71.46) * mm, "end": v(-33.58, 70.73) * mm});
            skLineSegment(sketch, "E662", {"start": v(-33.58, 70.73) * mm, "end": v(-34.5, 68.34) * mm});
            skLineSegment(sketch, "E663", {"start": v(-27.91, 65.83) * mm, "end": v(-27, 68.22) * mm});
            skLineSegment(sketch, "E664", {"start": v(-27, 68.22) * mm, "end": v(-29.03, 71.01) * mm});
            skLineSegment(sketch, "E665", {"start": v(-29.55, 70.87) * mm, "end": v(-29.9, 67.44) * mm});
            skLineSegment(sketch, "E666", {"start": v(-29.9, 67.44) * mm, "end": v(-27.91, 65.83) * mm});
            skLineSegment(sketch, "E667", {"start": v(-28.79, 71.32) * mm, "end": v(-25.63, 69.92) * mm});
            skLineSegment(sketch, "E668", {"start": v(-25.63, 69.92) * mm, "end": v(-23.48, 71.32) * mm});
            skLineSegment(sketch, "E669", {"start": v(-28.76, 71.85) * mm, "end": v(-25.48, 72.92) * mm});
            skLineSegment(sketch, "E670", {"start": v(-25.48, 72.92) * mm, "end": v(-23.48, 71.32) * mm});
            skLineSegment(sketch, "E671", {"start": v(-27.33, 77.22) * mm, "end": v(-26.67, 74.75) * mm});
            skLineSegment(sketch, "E672", {"start": v(-26.67, 74.75) * mm, "end": v(-28.98, 72.18) * mm});
            skLineSegment(sketch, "E673", {"start": v(-29.48, 72.37) * mm, "end": v(-29.48, 75.82) * mm});
            skLineSegment(sketch, "E674", {"start": v(-29.48, 75.82) * mm, "end": v(-27.33, 77.22) * mm});
            skArc(sketch, "E675", {"start": v(-29.92, 71.01) * mm, "mid": v(-29.74, 70.92) * mm, "end": v(-29.55, 70.87) * mm});
            skArc(sketch, "E676.trimOffspring", {"start": v(-30.19, 71.85) * mm, "mid": v(-30.22, 71.66) * mm, "end": v(-30.2, 71.46) * mm});
            skArc(sketch, "E677.trimOffspring", {"start": v(-29.48, 72.37) * mm, "mid": v(-29.67, 72.34) * mm, "end": v(-29.85, 72.27) * mm});
            skArc(sketch, "E678.trimOffspring", {"start": v(-28.76, 71.85) * mm, "mid": v(-28.85, 72.03) * mm, "end": v(-28.98, 72.18) * mm});
            skArc(sketch, "E679.trimOffspring", {"start": v(-29.03, 71.01) * mm, "mid": v(-28.9, 71.15) * mm, "end": v(-28.79, 71.32) * mm});
            skLineSegment(sketch, "E680", {"start": v(-33.07, 74.52) * mm, "end": v(-32.85, 73.7) * mm});
            skLineSegment(sketch, "E681", {"start": v(-32.85, 73.7) * mm, "end": v(-31.51, 73.26) * mm});
            skLineSegment(sketch, "E682", {"start": v(-31.51, 73.26) * mm, "end": v(-32.22, 74.48) * mm});
            skLineSegment(sketch, "E683", {"start": v(-32.22, 74.48) * mm, "end": v(-33.07, 74.52) * mm});
            skLineSegment(sketch, "E684", {"start": v(-27.83, 75.93) * mm, "end": v(-27.6, 75.1) * mm});
            skLineSegment(sketch, "E685", {"start": v(-27.6, 75.1) * mm, "end": v(-28.54, 74.07) * mm});
            skLineSegment(sketch, "E686", {"start": v(-28.54, 74.07) * mm, "end": v(-28.54, 75.47) * mm});
            skLineSegment(sketch, "E687", {"start": v(-28.54, 75.47) * mm, "end": v(-27.83, 75.93) * mm});
            skLineSegment(sketch, "E688", {"start": v(-28.27, 67.16) * mm, "end": v(-27.97, 67.96) * mm});
            skLineSegment(sketch, "E689", {"start": v(-27.97, 67.96) * mm, "end": v(-28.8, 69.1) * mm});
            skLineSegment(sketch, "E690", {"start": v(-28.8, 69.1) * mm, "end": v(-28.94, 67.7) * mm});
            skLineSegment(sketch, "E691", {"start": v(-28.94, 67.7) * mm, "end": v(-28.27, 67.16) * mm});
            skLineSegment(sketch, "E692", {"start": v(-24.86, 71.39) * mm, "end": v(-25.53, 71.92) * mm});
            skLineSegment(sketch, "E693", {"start": v(-25.53, 71.92) * mm, "end": v(-26.86, 71.49) * mm});
            skLineSegment(sketch, "E694", {"start": v(-26.86, 71.49) * mm, "end": v(-25.58, 70.92) * mm});
            skLineSegment(sketch, "E695", {"start": v(-25.58, 70.92) * mm, "end": v(-24.86, 71.39) * mm});
            skLineSegment(sketch, "E696", {"start": v(-33.34, 69.1) * mm, "end": v(-32.5, 69.06) * mm});
            skLineSegment(sketch, "E697", {"start": v(-32.5, 69.06) * mm, "end": v(-31.67, 70.2) * mm});
            skLineSegment(sketch, "E698", {"start": v(-31.67, 70.2) * mm, "end": v(-33.04, 69.9) * mm});
            skLineSegment(sketch, "E699", {"start": v(-33.04, 69.9) * mm, "end": v(-33.34, 69.1) * mm});
            skLineSegment(sketch, "E700", {"start": v(-55.63, -68.55) * mm, "end": v(-53.1, -68.99) * mm});
            skLineSegment(sketch, "E701", {"start": v(-53.1, -68.99) * mm, "end": v(-50.75, -66.46) * mm});
            skLineSegment(sketch, "E702", {"start": v(-50.99, -65.98) * mm, "end": v(-54.43, -66.3) * mm});
            skLineSegment(sketch, "E703", {"start": v(-54.43, -66.3) * mm, "end": v(-55.63, -68.55) * mm});
            skLineSegment(sketch, "E704", {"start": v(-49.4, -71.85) * mm, "end": v(-48.2, -69.6) * mm});
            skLineSegment(sketch, "E705", {"start": v(-48.2, -69.6) * mm, "end": v(-49.88, -66.57) * mm});
            skLineSegment(sketch, "E706", {"start": v(-50.4, -66.65) * mm, "end": v(-51.17, -70.01) * mm});
            skLineSegment(sketch, "E707", {"start": v(-51.17, -70.01) * mm, "end": v(-49.4, -71.85) * mm});
            skLineSegment(sketch, "E708", {"start": v(-44.33, -66.95) * mm, "end": v(-46.12, -65.11) * mm});
            skLineSegment(sketch, "E709", {"start": v(-46.12, -65.11) * mm, "end": v(-49.5, -65.77) * mm});
            skLineSegment(sketch, "E710", {"start": v(-49.6, -66.3) * mm, "end": v(-46.63, -68.07) * mm});
            skLineSegment(sketch, "E711", {"start": v(-46.63, -68.07) * mm, "end": v(-44.33, -66.95) * mm});
            skLineSegment(sketch, "E712", {"start": v(-49.68, -65.42) * mm, "end": v(-47.08, -63.15) * mm});
            skLineSegment(sketch, "E713", {"start": v(-47.08, -63.15) * mm, "end": v(-47.43, -60.61) * mm});
            skLineSegment(sketch, "E714", {"start": v(-50.15, -65.17) * mm, "end": v(-49.73, -61.74) * mm});
            skLineSegment(sketch, "E715", {"start": v(-49.73, -61.74) * mm, "end": v(-47.43, -60.61) * mm});
            skLineSegment(sketch, "E716", {"start": v(-54.42, -61.6) * mm, "end": v(-51.9, -62.05) * mm});
            skLineSegment(sketch, "E717", {"start": v(-51.9, -62.05) * mm, "end": v(-50.54, -65.22) * mm});
            skLineSegment(sketch, "E718", {"start": v(-50.92, -65.6) * mm, "end": v(-54.05, -64.14) * mm});
            skLineSegment(sketch, "E719", {"start": v(-54.05, -64.14) * mm, "end": v(-54.42, -61.6) * mm});
            skArc(sketch, "E720", {"start": v(-49.88, -66.57) * mm, "mid": v(-49.72, -66.45) * mm, "end": v(-49.6, -66.3) * mm});
            skArc(sketch, "E721.trimOffspring", {"start": v(-50.75, -66.46) * mm, "mid": v(-50.6, -66.58) * mm, "end": v(-50.4, -66.65) * mm});
            skArc(sketch, "E722.trimOffspring", {"start": v(-50.92, -65.6) * mm, "mid": v(-50.98, -65.78) * mm, "end": v(-50.99, -65.98) * mm});
            skArc(sketch, "E723.trimOffspring", {"start": v(-50.15, -65.17) * mm, "mid": v(-50.35, -65.17) * mm, "end": v(-50.54, -65.22) * mm});
            skArc(sketch, "E724.trimOffspring", {"start": v(-49.5, -65.77) * mm, "mid": v(-49.57, -65.58) * mm, "end": v(-49.68, -65.42) * mm});
            skLineSegment(sketch, "E725", {"start": v(-54.39, -67.95) * mm, "end": v(-53.55, -68.1) * mm});
            skLineSegment(sketch, "E726", {"start": v(-53.55, -68.1) * mm, "end": v(-52.6, -67.07) * mm});
            skLineSegment(sketch, "E727", {"start": v(-52.6, -67.07) * mm, "end": v(-53.99, -67.2) * mm});
            skLineSegment(sketch, "E728", {"start": v(-53.99, -67.2) * mm, "end": v(-54.39, -67.95) * mm});
            skLineSegment(sketch, "E729", {"start": v(-53.46, -62.6) * mm, "end": v(-52.62, -62.75) * mm});
            skLineSegment(sketch, "E730", {"start": v(-52.62, -62.75) * mm, "end": v(-52.06, -64.03) * mm});
            skLineSegment(sketch, "E731", {"start": v(-52.06, -64.03) * mm, "end": v(-53.33, -63.44) * mm});
            skLineSegment(sketch, "E732", {"start": v(-53.33, -63.44) * mm, "end": v(-53.46, -62.6) * mm});
            skLineSegment(sketch, "E733", {"start": v(-45.7, -66.7) * mm, "end": v(-46.29, -66.1) * mm});
            skLineSegment(sketch, "E734", {"start": v(-46.29, -66.1) * mm, "end": v(-47.66, -66.36) * mm});
            skLineSegment(sketch, "E735", {"start": v(-47.66, -66.36) * mm, "end": v(-46.46, -67.08) * mm});
            skLineSegment(sketch, "E736", {"start": v(-46.46, -67.08) * mm, "end": v(-45.7, -66.7) * mm});
            skLineSegment(sketch, "E737", {"start": v(-48.08, -61.83) * mm, "end": v(-48.85, -62.2) * mm});
            skLineSegment(sketch, "E738", {"start": v(-48.85, -62.2) * mm, "end": v(-49.02, -63.6) * mm});
            skLineSegment(sketch, "E739", {"start": v(-49.02, -63.6) * mm, "end": v(-47.96, -62.68) * mm});
            skLineSegment(sketch, "E740", {"start": v(-47.96, -62.68) * mm, "end": v(-48.08, -61.83) * mm});
            skLineSegment(sketch, "E741", {"start": v(-49.6, -70.49) * mm, "end": v(-49.2, -69.73) * mm});
            skLineSegment(sketch, "E742", {"start": v(-49.2, -69.73) * mm, "end": v(-49.87, -68.5) * mm});
            skLineSegment(sketch, "E743", {"start": v(-49.87, -68.5) * mm, "end": v(-50.18, -69.87) * mm});
            skLineSegment(sketch, "E744", {"start": v(-50.18, -69.87) * mm, "end": v(-49.6, -70.49) * mm});
            skLineSegment(sketch, "E745", {"start": v(40.59, -64.4) * mm, "end": v(42.55, -66.04) * mm});
            skLineSegment(sketch, "E746", {"start": v(42.55, -66.04) * mm, "end": v(45.86, -65.03) * mm});
            skLineSegment(sketch, "E747", {"start": v(45.9, -64.5) * mm, "end": v(42.76, -63.05) * mm});
            skLineSegment(sketch, "E748", {"start": v(42.76, -63.05) * mm, "end": v(40.59, -64.4) * mm});
            skLineSegment(sketch, "E749", {"start": v(44.34, -70.38) * mm, "end": v(46.5, -69.01) * mm});
            skLineSegment(sketch, "E750", {"start": v(46.5, -69.01) * mm, "end": v(46.56, -65.56) * mm});
            skLineSegment(sketch, "E751", {"start": v(46.07, -65.36) * mm, "end": v(43.72, -67.9) * mm});
            skLineSegment(sketch, "E752", {"start": v(43.72, -67.9) * mm, "end": v(44.34, -70.38) * mm});
            skLineSegment(sketch, "E753", {"start": v(51.18, -68.66) * mm, "end": v(50.55, -66.18) * mm});
            skLineSegment(sketch, "E754", {"start": v(50.55, -66.18) * mm, "end": v(47.28, -65.05) * mm});
            skLineSegment(sketch, "E755", {"start": v(46.94, -65.46) * mm, "end": v(48.62, -68.48) * mm});
            skLineSegment(sketch, "E756", {"start": v(48.62, -68.48) * mm, "end": v(51.18, -68.66) * mm});
            skLineSegment(sketch, "E757", {"start": v(47.31, -64.66) * mm, "end": v(50.7, -64) * mm});
            skLineSegment(sketch, "E758", {"start": v(50.7, -64) * mm, "end": v(51.66, -61.62) * mm});
            skLineSegment(sketch, "E759", {"start": v(47.03, -64.21) * mm, "end": v(49.1, -61.45) * mm});
            skLineSegment(sketch, "E760", {"start": v(49.1, -61.45) * mm, "end": v(51.66, -61.62) * mm});
            skLineSegment(sketch, "E761", {"start": v(45.11, -58.99) * mm, "end": v(47.07, -60.64) * mm});
            skLineSegment(sketch, "E762", {"start": v(47.07, -60.64) * mm, "end": v(46.66, -64.06) * mm});
            skLineSegment(sketch, "E763", {"start": v(46.14, -64.2) * mm, "end": v(44.16, -61.37) * mm});
            skLineSegment(sketch, "E764", {"start": v(44.16, -61.37) * mm, "end": v(45.11, -58.99) * mm});
            skArc(sketch, "E765", {"start": v(46.56, -65.56) * mm, "mid": v(46.76, -65.54) * mm, "end": v(46.94, -65.46) * mm});
            skArc(sketch, "E766.trimOffspring", {"start": v(45.86, -65.03) * mm, "mid": v(45.94, -65.2) * mm, "end": v(46.07, -65.36) * mm});
            skArc(sketch, "E767.trimOffspring", {"start": v(46.14, -64.2) * mm, "mid": v(46, -64.33) * mm, "end": v(45.9, -64.5) * mm});
            skArc(sketch, "E768.trimOffspring", {"start": v(47.03, -64.21) * mm, "mid": v(46.85, -64.11) * mm, "end": v(46.66, -64.06) * mm});
            skArc(sketch, "E769.trimOffspring", {"start": v(47.28, -65.05) * mm, "mid": v(47.32, -64.86) * mm, "end": v(47.31, -64.66) * mm});
            skLineSegment(sketch, "E770", {"start": v(41.97, -64.5) * mm, "end": v(42.62, -65.04) * mm});
            skLineSegment(sketch, "E771", {"start": v(42.62, -65.04) * mm, "end": v(43.96, -64.63) * mm});
            skLineSegment(sketch, "E772", {"start": v(43.96, -64.63) * mm, "end": v(42.7, -64.04) * mm});
            skLineSegment(sketch, "E773", {"start": v(42.7, -64.04) * mm, "end": v(41.97, -64.5) * mm});
            skLineSegment(sketch, "E774", {"start": v(45.45, -60.33) * mm, "end": v(46.1, -60.88) * mm});
            skLineSegment(sketch, "E775", {"start": v(46.1, -60.88) * mm, "end": v(45.94, -62.27) * mm});
            skLineSegment(sketch, "E776", {"start": v(45.94, -62.27) * mm, "end": v(45.13, -61.12) * mm});
            skLineSegment(sketch, "E777", {"start": v(45.13, -61.12) * mm, "end": v(45.45, -60.33) * mm});
            skLineSegment(sketch, "E778", {"start": v(50.12, -67.77) * mm, "end": v(49.9, -66.94) * mm});
            skLineSegment(sketch, "E779", {"start": v(49.9, -66.94) * mm, "end": v(48.58, -66.49) * mm});
            skLineSegment(sketch, "E780", {"start": v(48.58, -66.49) * mm, "end": v(49.27, -67.71) * mm});
            skLineSegment(sketch, "E781", {"start": v(49.27, -67.71) * mm, "end": v(50.12, -67.77) * mm});
            skLineSegment(sketch, "E782", {"start": v(50.49, -62.36) * mm, "end": v(49.64, -62.3) * mm});
            skLineSegment(sketch, "E783", {"start": v(49.64, -62.3) * mm, "end": v(48.8, -63.42) * mm});
            skLineSegment(sketch, "E784", {"start": v(48.8, -63.42) * mm, "end": v(50.17, -63.15) * mm});
            skLineSegment(sketch, "E785", {"start": v(50.17, -63.15) * mm, "end": v(50.49, -62.36) * mm});
            skLineSegment(sketch, "E786", {"start": v(44.85, -69.1) * mm, "end": v(45.57, -68.64) * mm});
            skLineSegment(sketch, "E787", {"start": v(45.57, -68.64) * mm, "end": v(45.6, -67.24) * mm});
            skLineSegment(sketch, "E788", {"start": v(45.6, -67.24) * mm, "end": v(44.65, -68.27) * mm});
            skLineSegment(sketch, "E789", {"start": v(44.65, -68.27) * mm, "end": v(44.85, -69.1) * mm});
            skLineSegment(sketch, "E790", {"start": v(-36.1, -64.7) * mm, "end": v(-35.42, -67.16) * mm});
            skLineSegment(sketch, "E791", {"start": v(-35.42, -67.16) * mm, "end": v(-32.13, -68.23) * mm});
            skLineSegment(sketch, "E792", {"start": v(-31.8, -67.81) * mm, "end": v(-33.54, -64.83) * mm});
            skLineSegment(sketch, "E793", {"start": v(-33.54, -64.83) * mm, "end": v(-36.1, -64.7) * mm});
            skLineSegment(sketch, "E794", {"start": v(-36.45, -71.74) * mm, "end": v(-33.9, -71.86) * mm});
            skLineSegment(sketch, "E795", {"start": v(-33.9, -71.86) * mm, "end": v(-31.86, -69.07) * mm});
            skLineSegment(sketch, "E796", {"start": v(-32.15, -68.62) * mm, "end": v(-35.53, -69.35) * mm});
            skLineSegment(sketch, "E797", {"start": v(-35.53, -69.35) * mm, "end": v(-36.45, -71.74) * mm});
            skLineSegment(sketch, "E798", {"start": v(-29.86, -74.26) * mm, "end": v(-28.95, -71.86) * mm});
            skLineSegment(sketch, "E799", {"start": v(-28.95, -71.86) * mm, "end": v(-30.98, -69.07) * mm});
            skLineSegment(sketch, "E800", {"start": v(-31.5, -69.2) * mm, "end": v(-31.85, -72.65) * mm});
            skLineSegment(sketch, "E801", {"start": v(-31.85, -72.65) * mm, "end": v(-29.86, -74.26) * mm});
            skLineSegment(sketch, "E802", {"start": v(-30.74, -68.77) * mm, "end": v(-27.58, -70.16) * mm});
            skLineSegment(sketch, "E803", {"start": v(-27.58, -70.16) * mm, "end": v(-25.43, -68.77) * mm});
            skLineSegment(sketch, "E804", {"start": v(-30.7, -68.23) * mm, "end": v(-27.42, -67.16) * mm});
            skLineSegment(sketch, "E805", {"start": v(-27.42, -67.16) * mm, "end": v(-25.43, -68.77) * mm});
            skLineSegment(sketch, "E806", {"start": v(-29.28, -62.86) * mm, "end": v(-28.62, -65.33) * mm});
            skLineSegment(sketch, "E807", {"start": v(-28.62, -65.33) * mm, "end": v(-30.92, -67.9) * mm});
            skLineSegment(sketch, "E808", {"start": v(-31.42, -67.71) * mm, "end": v(-31.42, -64.26) * mm});
            skLineSegment(sketch, "E809", {"start": v(-31.42, -64.26) * mm, "end": v(-29.28, -62.86) * mm});
            skArc(sketch, "E810", {"start": v(-31.86, -69.07) * mm, "mid": v(-31.69, -69.16) * mm, "end": v(-31.5, -69.2) * mm});
            skArc(sketch, "E811.trimOffspring", {"start": v(-32.13, -68.23) * mm, "mid": v(-32.17, -68.43) * mm, "end": v(-32.15, -68.62) * mm});
            skArc(sketch, "E812.trimOffspring", {"start": v(-31.42, -67.71) * mm, "mid": v(-31.62, -67.74) * mm, "end": v(-31.8, -67.81) * mm});
            skArc(sketch, "E813.trimOffspring", {"start": v(-30.7, -68.23) * mm, "mid": v(-30.8, -68.05) * mm, "end": v(-30.92, -67.9) * mm});
            skArc(sketch, "E814.trimOffspring", {"start": v(-30.98, -69.07) * mm, "mid": v(-30.84, -68.93) * mm, "end": v(-30.74, -68.77) * mm});
            skLineSegment(sketch, "E815", {"start": v(-35.01, -65.56) * mm, "end": v(-34.8, -66.39) * mm});
            skLineSegment(sketch, "E816", {"start": v(-34.8, -66.39) * mm, "end": v(-33.46, -66.82) * mm});
            skLineSegment(sketch, "E817", {"start": v(-33.46, -66.82) * mm, "end": v(-34.16, -65.6) * mm});
            skLineSegment(sketch, "E818", {"start": v(-34.16, -65.6) * mm, "end": v(-35.01, -65.56) * mm});
            skLineSegment(sketch, "E819", {"start": v(-29.77, -64.15) * mm, "end": v(-29.55, -64.97) * mm});
            skLineSegment(sketch, "E820", {"start": v(-29.55, -64.97) * mm, "end": v(-30.49, -66.02) * mm});
            skLineSegment(sketch, "E821", {"start": v(-30.49, -66.02) * mm, "end": v(-30.49, -64.62) * mm});
            skLineSegment(sketch, "E822", {"start": v(-30.49, -64.62) * mm, "end": v(-29.77, -64.15) * mm});
            skLineSegment(sketch, "E823", {"start": v(-30.22, -72.92) * mm, "end": v(-29.92, -72.12) * mm});
            skLineSegment(sketch, "E824", {"start": v(-29.92, -72.12) * mm, "end": v(-30.74, -71) * mm});
            skLineSegment(sketch, "E825", {"start": v(-30.74, -71) * mm, "end": v(-30.88, -72.38) * mm});
            skLineSegment(sketch, "E826", {"start": v(-30.88, -72.38) * mm, "end": v(-30.22, -72.92) * mm});
            skLineSegment(sketch, "E827", {"start": v(-26.8, -68.7) * mm, "end": v(-27.47, -68.16) * mm});
            skLineSegment(sketch, "E828", {"start": v(-27.47, -68.16) * mm, "end": v(-28.8, -68.6) * mm});
            skLineSegment(sketch, "E829", {"start": v(-28.8, -68.6) * mm, "end": v(-27.52, -69.16) * mm});
            skLineSegment(sketch, "E830", {"start": v(-27.52, -69.16) * mm, "end": v(-26.8, -68.7) * mm});
            skLineSegment(sketch, "E831", {"start": v(-35.3, -70.98) * mm, "end": v(-34.44, -71.03) * mm});
            skLineSegment(sketch, "E832", {"start": v(-34.44, -71.03) * mm, "end": v(-33.61, -69.9) * mm});
            skLineSegment(sketch, "E833", {"start": v(-33.61, -69.9) * mm, "end": v(-34.98, -70.19) * mm});
            skLineSegment(sketch, "E834", {"start": v(-34.98, -70.19) * mm, "end": v(-35.3, -70.98) * mm});
            skLineSegment(sketch, "E835", {"start": v(-68.1, -64.5) * mm, "end": v(-68.09, -67.05) * mm});
            skLineSegment(sketch, "E836", {"start": v(-68.09, -67.05) * mm, "end": v(-65.19, -68.93) * mm});
            skLineSegment(sketch, "E837", {"start": v(-64.76, -68.62) * mm, "end": v(-65.66, -65.28) * mm});
            skLineSegment(sketch, "E838", {"start": v(-65.66, -65.28) * mm, "end": v(-68.1, -64.5) * mm});
            skLineSegment(sketch, "E839", {"start": v(-70.26, -71.2) * mm, "end": v(-67.83, -71.99) * mm});
            skLineSegment(sketch, "E840", {"start": v(-67.83, -71.99) * mm, "end": v(-65.14, -69.81) * mm});
            skLineSegment(sketch, "E841", {"start": v(-65.3, -69.3) * mm, "end": v(-68.76, -69.14) * mm});
            skLineSegment(sketch, "E842", {"start": v(-68.76, -69.14) * mm, "end": v(-70.26, -71.2) * mm});
            skLineSegment(sketch, "E843", {"start": v(-64.55, -75.34) * mm, "end": v(-63.05, -73.27) * mm});
            skLineSegment(sketch, "E844", {"start": v(-63.05, -73.27) * mm, "end": v(-64.3, -70.04) * mm});
            skLineSegment(sketch, "E845", {"start": v(-64.83, -70.04) * mm, "end": v(-66.05, -73.27) * mm});
            skLineSegment(sketch, "E846", {"start": v(-66.05, -73.27) * mm, "end": v(-64.55, -75.34) * mm});
            skLineSegment(sketch, "E847", {"start": v(-63.98, -69.81) * mm, "end": v(-61.28, -71.98) * mm});
            skLineSegment(sketch, "E848", {"start": v(-61.28, -71.98) * mm, "end": v(-58.85, -71.19) * mm});
            skLineSegment(sketch, "E849", {"start": v(-63.81, -69.3) * mm, "end": v(-60.36, -69.12) * mm});
            skLineSegment(sketch, "E850", {"start": v(-60.36, -69.12) * mm, "end": v(-58.85, -71.19) * mm});
            skLineSegment(sketch, "E851", {"start": v(-61.04, -64.48) * mm, "end": v(-61.04, -67.04) * mm});
            skLineSegment(sketch, "E852", {"start": v(-61.04, -67.04) * mm, "end": v(-63.93, -68.93) * mm});
            skLineSegment(sketch, "E853", {"start": v(-64.37, -68.62) * mm, "end": v(-63.47, -65.28) * mm});
            skLineSegment(sketch, "E854", {"start": v(-63.47, -65.28) * mm, "end": v(-61.04, -64.48) * mm});
            skArc(sketch, "E855", {"start": v(-65.14, -69.81) * mm, "mid": v(-65, -69.95) * mm, "end": v(-64.83, -70.04) * mm});
            skArc(sketch, "E856.trimOffspring", {"start": v(-65.19, -68.93) * mm, "mid": v(-65.27, -69.11) * mm, "end": v(-65.3, -69.3) * mm});
            skArc(sketch, "E857.trimOffspring", {"start": v(-64.37, -68.62) * mm, "mid": v(-64.56, -68.6) * mm, "end": v(-64.76, -68.62) * mm});
            skArc(sketch, "E858.trimOffspring", {"start": v(-63.81, -69.3) * mm, "mid": v(-63.85, -69.1) * mm, "end": v(-63.93, -68.93) * mm});
            skArc(sketch, "E859.trimOffspring", {"start": v(-64.3, -70.04) * mm, "mid": v(-64.12, -69.95) * mm, "end": v(-63.98, -69.81) * mm});
            skLineSegment(sketch, "E860", {"start": v(-67.28, -65.61) * mm, "end": v(-67.28, -66.46) * mm});
            skLineSegment(sketch, "E861", {"start": v(-67.28, -66.46) * mm, "end": v(-66.1, -67.23) * mm});
            skLineSegment(sketch, "E862", {"start": v(-66.1, -67.23) * mm, "end": v(-66.47, -65.87) * mm});
            skLineSegment(sketch, "E863", {"start": v(-66.47, -65.87) * mm, "end": v(-67.28, -65.61) * mm});
            skLineSegment(sketch, "E864", {"start": v(-61.85, -65.6) * mm, "end": v(-61.85, -66.45) * mm});
            skLineSegment(sketch, "E865", {"start": v(-61.85, -66.45) * mm, "end": v(-63.03, -67.22) * mm});
            skLineSegment(sketch, "E866", {"start": v(-63.03, -67.22) * mm, "end": v(-62.66, -65.87) * mm});
            skLineSegment(sketch, "E867", {"start": v(-62.66, -65.87) * mm, "end": v(-61.85, -65.6) * mm});
            skLineSegment(sketch, "E868", {"start": v(-64.55, -73.96) * mm, "end": v(-64.05, -73.27) * mm});
            skLineSegment(sketch, "E869", {"start": v(-64.05, -73.27) * mm, "end": v(-64.56, -71.96) * mm});
            skLineSegment(sketch, "E870", {"start": v(-64.56, -71.96) * mm, "end": v(-65.05, -73.27) * mm});
            skLineSegment(sketch, "E871", {"start": v(-65.05, -73.27) * mm, "end": v(-64.55, -73.96) * mm});
            skLineSegment(sketch, "E872", {"start": v(-60.17, -70.76) * mm, "end": v(-60.67, -70.07) * mm});
            skLineSegment(sketch, "E873", {"start": v(-60.67, -70.07) * mm, "end": v(-62.07, -70.15) * mm});
            skLineSegment(sketch, "E874", {"start": v(-62.07, -70.15) * mm, "end": v(-60.98, -71.03) * mm});
            skLineSegment(sketch, "E875", {"start": v(-60.98, -71.03) * mm, "end": v(-60.17, -70.76) * mm});
            skLineSegment(sketch, "E876", {"start": v(-68.95, -70.78) * mm, "end": v(-68.14, -71.04) * mm});
            skLineSegment(sketch, "E877", {"start": v(-68.14, -71.04) * mm, "end": v(-67.05, -70.15) * mm});
            skLineSegment(sketch, "E878", {"start": v(-67.05, -70.15) * mm, "end": v(-68.45, -70.09) * mm});
            skLineSegment(sketch, "E879", {"start": v(-68.45, -70.09) * mm, "end": v(-68.95, -70.78) * mm});
            skLineSegment(sketch, "E880", {"start": v(6.23, -62.89) * mm, "end": v(6.9, -65.36) * mm});
            skLineSegment(sketch, "E881", {"start": v(6.9, -65.36) * mm, "end": v(10.18, -66.42) * mm});
            skLineSegment(sketch, "E882", {"start": v(10.52, -66) * mm, "end": v(8.78, -63.02) * mm});
            skLineSegment(sketch, "E883", {"start": v(8.78, -63.02) * mm, "end": v(6.23, -62.89) * mm});
            skLineSegment(sketch, "E884", {"start": v(5.87, -69.93) * mm, "end": v(8.42, -70.06) * mm});
            skLineSegment(sketch, "E885", {"start": v(8.42, -70.06) * mm, "end": v(10.45, -67.26) * mm});
            skLineSegment(sketch, "E886", {"start": v(10.16, -66.81) * mm, "end": v(6.79, -67.54) * mm});
            skLineSegment(sketch, "E887", {"start": v(6.79, -67.54) * mm, "end": v(5.87, -69.93) * mm});
            skLineSegment(sketch, "E888", {"start": v(12.46, -72.45) * mm, "end": v(13.37, -70.06) * mm});
            skLineSegment(sketch, "E889", {"start": v(13.37, -70.06) * mm, "end": v(11.34, -67.26) * mm});
            skLineSegment(sketch, "E890", {"start": v(10.82, -67.4) * mm, "end": v(10.47, -70.84) * mm});
            skLineSegment(sketch, "E891", {"start": v(10.47, -70.84) * mm, "end": v(12.46, -72.45) * mm});
            skLineSegment(sketch, "E892", {"start": v(11.58, -66.96) * mm, "end": v(14.74, -68.35) * mm});
            skLineSegment(sketch, "E893", {"start": v(14.74, -68.35) * mm, "end": v(16.89, -66.96) * mm});
            skLineSegment(sketch, "E894", {"start": v(11.6, -66.42) * mm, "end": v(14.9, -65.36) * mm});
            skLineSegment(sketch, "E895", {"start": v(14.9, -65.36) * mm, "end": v(16.89, -66.96) * mm});
            skLineSegment(sketch, "E896", {"start": v(13.04, -61.05) * mm, "end": v(13.7, -63.52) * mm});
            skLineSegment(sketch, "E897", {"start": v(13.7, -63.52) * mm, "end": v(11.4, -66.1) * mm});
            skLineSegment(sketch, "E898", {"start": v(10.9, -65.9) * mm, "end": v(10.9, -62.45) * mm});
            skLineSegment(sketch, "E899", {"start": v(10.9, -62.45) * mm, "end": v(13.04, -61.05) * mm});
            skArc(sketch, "E900", {"start": v(10.45, -67.26) * mm, "mid": v(10.63, -67.36) * mm, "end": v(10.82, -67.4) * mm});
            skArc(sketch, "E901.trimOffspring", {"start": v(10.18, -66.42) * mm, "mid": v(10.15, -66.62) * mm, "end": v(10.16, -66.81) * mm});
            skArc(sketch, "E902.trimOffspring", {"start": v(10.9, -65.9) * mm, "mid": v(10.7, -65.93) * mm, "end": v(10.52, -66) * mm});
            skArc(sketch, "E903.trimOffspring", {"start": v(11.6, -66.42) * mm, "mid": v(11.52, -66.25) * mm, "end": v(11.4, -66.1) * mm});
            skArc(sketch, "E904.trimOffspring", {"start": v(11.34, -67.26) * mm, "mid": v(11.48, -67.13) * mm, "end": v(11.58, -66.96) * mm});
            skLineSegment(sketch, "E905", {"start": v(7.3, -63.76) * mm, "end": v(7.53, -64.58) * mm});
            skLineSegment(sketch, "E906", {"start": v(7.53, -64.58) * mm, "end": v(8.86, -65.01) * mm});
            skLineSegment(sketch, "E907", {"start": v(8.86, -65.01) * mm, "end": v(8.15, -63.8) * mm});
            skLineSegment(sketch, "E908", {"start": v(8.15, -63.8) * mm, "end": v(7.3, -63.76) * mm});
            skLineSegment(sketch, "E909", {"start": v(12.54, -62.34) * mm, "end": v(12.76, -63.17) * mm});
            skLineSegment(sketch, "E910", {"start": v(12.76, -63.17) * mm, "end": v(11.83, -64.21) * mm});
            skLineSegment(sketch, "E911", {"start": v(11.83, -64.21) * mm, "end": v(11.83, -62.8) * mm});
            skLineSegment(sketch, "E912", {"start": v(11.83, -62.8) * mm, "end": v(12.54, -62.34) * mm});
            skLineSegment(sketch, "E913", {"start": v(12.1, -71.11) * mm, "end": v(12.4, -70.32) * mm});
            skLineSegment(sketch, "E914", {"start": v(12.4, -70.32) * mm, "end": v(11.58, -69.18) * mm});
            skLineSegment(sketch, "E915", {"start": v(11.58, -69.18) * mm, "end": v(11.44, -70.58) * mm});
            skLineSegment(sketch, "E916", {"start": v(11.44, -70.58) * mm, "end": v(12.1, -71.11) * mm});
            skLineSegment(sketch, "E917", {"start": v(15.5, -66.9) * mm, "end": v(14.84, -66.36) * mm});
            skLineSegment(sketch, "E918", {"start": v(14.84, -66.36) * mm, "end": v(13.5, -66.79) * mm});
            skLineSegment(sketch, "E919", {"start": v(13.5, -66.79) * mm, "end": v(14.8, -67.36) * mm});
            skLineSegment(sketch, "E920", {"start": v(14.8, -67.36) * mm, "end": v(15.5, -66.9) * mm});
            skLineSegment(sketch, "E921", {"start": v(7.03, -69.18) * mm, "end": v(7.88, -69.22) * mm});
            skLineSegment(sketch, "E922", {"start": v(7.88, -69.22) * mm, "end": v(8.7, -68.09) * mm});
            skLineSegment(sketch, "E923", {"start": v(8.7, -68.09) * mm, "end": v(7.33, -68.38) * mm});
            skLineSegment(sketch, "E924", {"start": v(7.33, -68.38) * mm, "end": v(7.03, -69.18) * mm});
            skLineSegment(sketch, "E925", {"start": v(84.06, 45.44) * mm, "end": v(84.73, 42.98) * mm});
            skLineSegment(sketch, "E926", {"start": v(84.73, 42.98) * mm, "end": v(88.01, 41.9) * mm});
            skLineSegment(sketch, "E927", {"start": v(88.35, 42.32) * mm, "end": v(86.61, 45.3) * mm});
            skLineSegment(sketch, "E928", {"start": v(86.61, 45.3) * mm, "end": v(84.06, 45.44) * mm});
            skLineSegment(sketch, "E929", {"start": v(83.7, 38.4) * mm, "end": v(86.25, 38.28) * mm});
            skLineSegment(sketch, "E930", {"start": v(86.25, 38.28) * mm, "end": v(88.28, 41.07) * mm});
            skLineSegment(sketch, "E931", {"start": v(88, 41.52) * mm, "end": v(84.62, 40.79) * mm});
            skLineSegment(sketch, "E932", {"start": v(84.62, 40.79) * mm, "end": v(83.7, 38.4) * mm});
            skLineSegment(sketch, "E933", {"start": v(90.29, 35.88) * mm, "end": v(91.2, 38.28) * mm});
            skLineSegment(sketch, "E934", {"start": v(91.2, 38.28) * mm, "end": v(89.17, 41.07) * mm});
            skLineSegment(sketch, "E935", {"start": v(88.65, 40.93) * mm, "end": v(88.3, 37.5) * mm});
            skLineSegment(sketch, "E936", {"start": v(88.3, 37.5) * mm, "end": v(90.29, 35.88) * mm});
            skLineSegment(sketch, "E937", {"start": v(89.41, 41.37) * mm, "end": v(92.57, 39.98) * mm});
            skLineSegment(sketch, "E938", {"start": v(92.57, 39.98) * mm, "end": v(94.72, 41.37) * mm});
            skLineSegment(sketch, "E939", {"start": v(89.44, 41.9) * mm, "end": v(92.72, 42.98) * mm});
            skLineSegment(sketch, "E940", {"start": v(92.72, 42.98) * mm, "end": v(94.72, 41.37) * mm});
            skLineSegment(sketch, "E941", {"start": v(90.87, 47.28) * mm, "end": v(91.53, 44.8) * mm});
            skLineSegment(sketch, "E942", {"start": v(91.53, 44.8) * mm, "end": v(89.23, 42.24) * mm});
            skLineSegment(sketch, "E943", {"start": v(88.73, 42.43) * mm, "end": v(88.73, 45.88) * mm});
            skLineSegment(sketch, "E944", {"start": v(88.73, 45.88) * mm, "end": v(90.87, 47.28) * mm});
            skArc(sketch, "E945", {"start": v(88.28, 41.07) * mm, "mid": v(88.46, 40.98) * mm, "end": v(88.65, 40.93) * mm});
            skArc(sketch, "E946.trimOffspring", {"start": v(88.01, 41.9) * mm, "mid": v(87.98, 41.71) * mm, "end": v(88, 41.52) * mm});
            skArc(sketch, "E947.trimOffspring", {"start": v(88.73, 42.43) * mm, "mid": v(88.53, 42.4) * mm, "end": v(88.35, 42.32) * mm});
            skArc(sketch, "E948.trimOffspring", {"start": v(89.44, 41.9) * mm, "mid": v(89.35, 42.09) * mm, "end": v(89.23, 42.24) * mm});
            skArc(sketch, "E949.trimOffspring", {"start": v(89.17, 41.07) * mm, "mid": v(89.3, 41.2) * mm, "end": v(89.41, 41.37) * mm});
            skLineSegment(sketch, "E950", {"start": v(85.13, 44.58) * mm, "end": v(85.36, 43.75) * mm});
            skLineSegment(sketch, "E951", {"start": v(85.36, 43.75) * mm, "end": v(86.69, 43.32) * mm});
            skLineSegment(sketch, "E952", {"start": v(86.69, 43.32) * mm, "end": v(85.98, 44.53) * mm});
            skLineSegment(sketch, "E953", {"start": v(85.98, 44.53) * mm, "end": v(85.13, 44.58) * mm});
            skLineSegment(sketch, "E954", {"start": v(90.37, 46) * mm, "end": v(90.6, 45.17) * mm});
            skLineSegment(sketch, "E955", {"start": v(90.6, 45.17) * mm, "end": v(89.66, 44.12) * mm});
            skLineSegment(sketch, "E956", {"start": v(89.66, 44.12) * mm, "end": v(89.66, 45.52) * mm});
            skLineSegment(sketch, "E957", {"start": v(89.66, 45.52) * mm, "end": v(90.37, 46) * mm});
            skLineSegment(sketch, "E958", {"start": v(89.93, 37.22) * mm, "end": v(90.23, 38.01) * mm});
            skLineSegment(sketch, "E959", {"start": v(90.23, 38.01) * mm, "end": v(89.4, 39.15) * mm});
            skLineSegment(sketch, "E960", {"start": v(89.4, 39.15) * mm, "end": v(89.27, 37.75) * mm});
            skLineSegment(sketch, "E961", {"start": v(89.27, 37.75) * mm, "end": v(89.93, 37.22) * mm});
            skLineSegment(sketch, "E962", {"start": v(93.34, 41.44) * mm, "end": v(92.67, 41.98) * mm});
            skLineSegment(sketch, "E963", {"start": v(92.67, 41.98) * mm, "end": v(91.34, 41.54) * mm});
            skLineSegment(sketch, "E964", {"start": v(91.34, 41.54) * mm, "end": v(92.62, 40.98) * mm});
            skLineSegment(sketch, "E965", {"start": v(92.62, 40.98) * mm, "end": v(93.34, 41.44) * mm});
            skLineSegment(sketch, "E966", {"start": v(84.86, 39.15) * mm, "end": v(85.7, 39.11) * mm});
            skLineSegment(sketch, "E967", {"start": v(85.7, 39.11) * mm, "end": v(86.53, 40.25) * mm});
            skLineSegment(sketch, "E968", {"start": v(86.53, 40.25) * mm, "end": v(85.16, 39.95) * mm});
            skLineSegment(sketch, "E969", {"start": v(85.16, 39.95) * mm, "end": v(84.86, 39.15) * mm});
            skLineSegment(sketch, "E970", {"start": v(79.73, -28.84) * mm, "end": v(79.74, -31.4) * mm});
            skLineSegment(sketch, "E971", {"start": v(79.74, -31.4) * mm, "end": v(82.64, -33.28) * mm});
            skLineSegment(sketch, "E972", {"start": v(83.07, -32.97) * mm, "end": v(82.16, -29.64) * mm});
            skLineSegment(sketch, "E973", {"start": v(82.16, -29.64) * mm, "end": v(79.73, -28.84) * mm});
            skLineSegment(sketch, "E974", {"start": v(77.56, -35.56) * mm, "end": v(80, -36.34) * mm});
            skLineSegment(sketch, "E975", {"start": v(80, -36.34) * mm, "end": v(82.68, -34.16) * mm});
            skLineSegment(sketch, "E976", {"start": v(82.52, -33.66) * mm, "end": v(79.07, -33.49) * mm});
            skLineSegment(sketch, "E977", {"start": v(79.07, -33.49) * mm, "end": v(77.56, -35.56) * mm});
            skLineSegment(sketch, "E978", {"start": v(83.28, -39.7) * mm, "end": v(84.77, -37.62) * mm});
            skLineSegment(sketch, "E979", {"start": v(84.77, -37.62) * mm, "end": v(83.53, -34.4) * mm});
            skLineSegment(sketch, "E980", {"start": v(83, -34.4) * mm, "end": v(81.77, -37.62) * mm});
            skLineSegment(sketch, "E981", {"start": v(81.77, -37.62) * mm, "end": v(83.28, -39.7) * mm});
            skLineSegment(sketch, "E982", {"start": v(83.85, -34.16) * mm, "end": v(86.54, -36.33) * mm});
            skLineSegment(sketch, "E983", {"start": v(86.54, -36.33) * mm, "end": v(88.97, -35.54) * mm});
            skLineSegment(sketch, "E984", {"start": v(84.01, -33.65) * mm, "end": v(87.46, -33.47) * mm});
            skLineSegment(sketch, "E985", {"start": v(87.46, -33.47) * mm, "end": v(88.97, -35.54) * mm});
            skLineSegment(sketch, "E986", {"start": v(86.78, -28.83) * mm, "end": v(86.78, -31.4) * mm});
            skLineSegment(sketch, "E987", {"start": v(86.78, -31.4) * mm, "end": v(83.9, -33.28) * mm});
            skLineSegment(sketch, "E988", {"start": v(83.46, -32.97) * mm, "end": v(84.35, -29.63) * mm});
            skLineSegment(sketch, "E989", {"start": v(84.35, -29.63) * mm, "end": v(86.78, -28.83) * mm});
            skArc(sketch, "E990", {"start": v(82.68, -34.16) * mm, "mid": v(82.83, -34.3) * mm, "end": v(83, -34.4) * mm});
            skArc(sketch, "E991.trimOffspring", {"start": v(82.64, -33.28) * mm, "mid": v(82.55, -33.46) * mm, "end": v(82.52, -33.66) * mm});
            skArc(sketch, "E992.trimOffspring", {"start": v(83.46, -32.97) * mm, "mid": v(83.26, -32.94) * mm, "end": v(83.07, -32.97) * mm});
            skArc(sketch, "E993.trimOffspring", {"start": v(84.01, -33.65) * mm, "mid": v(83.98, -33.46) * mm, "end": v(83.9, -33.28) * mm});
            skArc(sketch, "E994.trimOffspring", {"start": v(83.53, -34.4) * mm, "mid": v(83.7, -34.3) * mm, "end": v(83.85, -34.16) * mm});
            skLineSegment(sketch, "E995", {"start": v(80.54, -29.96) * mm, "end": v(80.55, -30.81) * mm});
            skLineSegment(sketch, "E996", {"start": v(80.55, -30.81) * mm, "end": v(81.72, -31.58) * mm});
            skLineSegment(sketch, "E997", {"start": v(81.72, -31.58) * mm, "end": v(81.36, -30.22) * mm});
            skLineSegment(sketch, "E998", {"start": v(81.36, -30.22) * mm, "end": v(80.54, -29.96) * mm});
            skLineSegment(sketch, "E999", {"start": v(85.97, -29.95) * mm, "end": v(85.97, -30.8) * mm});
            skLineSegment(sketch, "E1000", {"start": v(85.97, -30.8) * mm, "end": v(84.8, -31.57) * mm});
            skLineSegment(sketch, "E1001", {"start": v(84.8, -31.57) * mm, "end": v(85.16, -30.22) * mm});
            skLineSegment(sketch, "E1002", {"start": v(85.16, -30.22) * mm, "end": v(85.97, -29.95) * mm});
            skLineSegment(sketch, "E1003", {"start": v(83.27, -38.31) * mm, "end": v(83.77, -37.62) * mm});
            skLineSegment(sketch, "E1004", {"start": v(83.77, -37.62) * mm, "end": v(83.27, -36.31) * mm});
            skLineSegment(sketch, "E1005", {"start": v(83.27, -36.31) * mm, "end": v(82.77, -37.62) * mm});
            skLineSegment(sketch, "E1006", {"start": v(82.77, -37.62) * mm, "end": v(83.27, -38.31) * mm});
            skLineSegment(sketch, "E1007", {"start": v(87.66, -35.11) * mm, "end": v(87.16, -34.42) * mm});
            skLineSegment(sketch, "E1008", {"start": v(87.16, -34.42) * mm, "end": v(85.76, -34.5) * mm});
            skLineSegment(sketch, "E1009", {"start": v(85.76, -34.5) * mm, "end": v(86.85, -35.38) * mm});
            skLineSegment(sketch, "E1010", {"start": v(86.85, -35.38) * mm, "end": v(87.66, -35.11) * mm});
            skLineSegment(sketch, "E1011", {"start": v(78.88, -35.13) * mm, "end": v(79.69, -35.39) * mm});
            skLineSegment(sketch, "E1012", {"start": v(79.69, -35.39) * mm, "end": v(80.78, -34.5) * mm});
            skLineSegment(sketch, "E1013", {"start": v(80.78, -34.5) * mm, "end": v(79.38, -34.44) * mm});
            skLineSegment(sketch, "E1014", {"start": v(79.38, -34.44) * mm, "end": v(78.88, -35.13) * mm});
            skLineSegment(sketch, "E1015", {"start": v(88.31, -47.38) * mm, "end": v(88.98, -49.85) * mm});
            skLineSegment(sketch, "E1016", {"start": v(88.98, -49.85) * mm, "end": v(92.27, -50.92) * mm});
            skLineSegment(sketch, "E1017", {"start": v(92.6, -50.5) * mm, "end": v(90.87, -47.52) * mm});
            skLineSegment(sketch, "E1018", {"start": v(90.87, -47.52) * mm, "end": v(88.31, -47.38) * mm});
            skLineSegment(sketch, "E1019", {"start": v(87.95, -54.43) * mm, "end": v(90.5, -54.55) * mm});
            skLineSegment(sketch, "E1020", {"start": v(90.5, -54.55) * mm, "end": v(92.54, -51.76) * mm});
            skLineSegment(sketch, "E1021", {"start": v(92.25, -51.3) * mm, "end": v(88.87, -52.04) * mm});
            skLineSegment(sketch, "E1022", {"start": v(88.87, -52.04) * mm, "end": v(87.95, -54.43) * mm});
            skLineSegment(sketch, "E1023", {"start": v(94.54, -56.94) * mm, "end": v(95.45, -54.55) * mm});
            skLineSegment(sketch, "E1024", {"start": v(95.45, -54.55) * mm, "end": v(93.42, -51.76) * mm});
            skLineSegment(sketch, "E1025", {"start": v(92.9, -51.9) * mm, "end": v(92.55, -55.33) * mm});
            skLineSegment(sketch, "E1026", {"start": v(92.55, -55.33) * mm, "end": v(94.54, -56.94) * mm});
            skLineSegment(sketch, "E1027", {"start": v(93.67, -51.45) * mm, "end": v(96.83, -52.85) * mm});
            skLineSegment(sketch, "E1028", {"start": v(96.83, -52.85) * mm, "end": v(98.97, -51.45) * mm});
            skLineSegment(sketch, "E1029", {"start": v(93.7, -50.92) * mm, "end": v(96.98, -49.85) * mm});
            skLineSegment(sketch, "E1030", {"start": v(96.98, -49.85) * mm, "end": v(98.97, -51.45) * mm});
            skLineSegment(sketch, "E1031", {"start": v(95.12, -45.55) * mm, "end": v(95.78, -48.02) * mm});
            skLineSegment(sketch, "E1032", {"start": v(95.78, -48.02) * mm, "end": v(93.48, -50.6) * mm});
            skLineSegment(sketch, "E1033", {"start": v(92.98, -50.4) * mm, "end": v(92.98, -46.95) * mm});
            skLineSegment(sketch, "E1034", {"start": v(92.98, -46.95) * mm, "end": v(95.12, -45.55) * mm});
            skArc(sketch, "E1035", {"start": v(92.54, -51.76) * mm, "mid": v(92.71, -51.85) * mm, "end": v(92.9, -51.9) * mm});
            skArc(sketch, "E1036.trimOffspring", {"start": v(92.27, -50.92) * mm, "mid": v(92.23, -51.11) * mm, "end": v(92.25, -51.3) * mm});
            skArc(sketch, "E1037.trimOffspring", {"start": v(92.98, -50.4) * mm, "mid": v(92.78, -50.43) * mm, "end": v(92.6, -50.5) * mm});
            skArc(sketch, "E1038.trimOffspring", {"start": v(93.7, -50.92) * mm, "mid": v(93.6, -50.74) * mm, "end": v(93.48, -50.6) * mm});
            skArc(sketch, "E1039.trimOffspring", {"start": v(93.42, -51.76) * mm, "mid": v(93.56, -51.62) * mm, "end": v(93.67, -51.45) * mm});
            skLineSegment(sketch, "E1040", {"start": v(89.39, -48.25) * mm, "end": v(89.6, -49.07) * mm});
            skLineSegment(sketch, "E1041", {"start": v(89.6, -49.07) * mm, "end": v(90.94, -49.5) * mm});
            skLineSegment(sketch, "E1042", {"start": v(90.94, -49.5) * mm, "end": v(90.24, -48.3) * mm});
            skLineSegment(sketch, "E1043", {"start": v(90.24, -48.3) * mm, "end": v(89.39, -48.25) * mm});
            skLineSegment(sketch, "E1044", {"start": v(94.63, -46.84) * mm, "end": v(94.85, -47.66) * mm});
            skLineSegment(sketch, "E1045", {"start": v(94.85, -47.66) * mm, "end": v(93.91, -48.7) * mm});
            skLineSegment(sketch, "E1046", {"start": v(93.91, -48.7) * mm, "end": v(93.91, -47.3) * mm});
            skLineSegment(sketch, "E1047", {"start": v(93.91, -47.3) * mm, "end": v(94.63, -46.84) * mm});
            skLineSegment(sketch, "E1048", {"start": v(94.18, -55.6) * mm, "end": v(94.49, -54.81) * mm});
            skLineSegment(sketch, "E1049", {"start": v(94.49, -54.81) * mm, "end": v(93.66, -53.68) * mm});
            skLineSegment(sketch, "E1050", {"start": v(93.66, -53.68) * mm, "end": v(93.52, -55.07) * mm});
            skLineSegment(sketch, "E1051", {"start": v(93.52, -55.07) * mm, "end": v(94.18, -55.6) * mm});
            skLineSegment(sketch, "E1052", {"start": v(97.6, -51.38) * mm, "end": v(96.93, -50.85) * mm});
            skLineSegment(sketch, "E1053", {"start": v(96.93, -50.85) * mm, "end": v(95.6, -51.28) * mm});
            skLineSegment(sketch, "E1054", {"start": v(95.6, -51.28) * mm, "end": v(96.88, -51.85) * mm});
            skLineSegment(sketch, "E1055", {"start": v(96.88, -51.85) * mm, "end": v(97.6, -51.38) * mm});
            skLineSegment(sketch, "E1056", {"start": v(89.11, -53.67) * mm, "end": v(89.96, -53.71) * mm});
            skLineSegment(sketch, "E1057", {"start": v(89.96, -53.71) * mm, "end": v(90.79, -52.58) * mm});
            skLineSegment(sketch, "E1058", {"start": v(90.79, -52.58) * mm, "end": v(89.42, -52.88) * mm});
            skLineSegment(sketch, "E1059", {"start": v(89.42, -52.88) * mm, "end": v(89.11, -53.67) * mm});
            skLineSegment(sketch, "E1060", {"start": v(77.85, -67.08) * mm, "end": v(78.94, -69.4) * mm});
            skLineSegment(sketch, "E1061", {"start": v(78.94, -69.4) * mm, "end": v(82.36, -69.88) * mm});
            skLineSegment(sketch, "E1062", {"start": v(82.62, -69.41) * mm, "end": v(80.4, -66.77) * mm});
            skLineSegment(sketch, "E1063", {"start": v(80.4, -66.77) * mm, "end": v(77.85, -67.08) * mm});
            skLineSegment(sketch, "E1064", {"start": v(78.72, -74.08) * mm, "end": v(81.26, -73.76) * mm});
            skLineSegment(sketch, "E1065", {"start": v(81.26, -73.76) * mm, "end": v(82.78, -70.66) * mm});
            skLineSegment(sketch, "E1066", {"start": v(82.41, -70.27) * mm, "end": v(79.21, -71.57) * mm});
            skLineSegment(sketch, "E1067", {"start": v(79.21, -71.57) * mm, "end": v(78.72, -74.08) * mm});
            skLineSegment(sketch, "E1068", {"start": v(85.65, -75.42) * mm, "end": v(86.13, -72.9) * mm});
            skLineSegment(sketch, "E1069", {"start": v(86.13, -72.9) * mm, "end": v(83.64, -70.5) * mm});
            skLineSegment(sketch, "E1070", {"start": v(83.16, -70.73) * mm, "end": v(83.41, -74.18) * mm});
            skLineSegment(sketch, "E1071", {"start": v(83.41, -74.18) * mm, "end": v(85.65, -75.42) * mm});
            skLineSegment(sketch, "E1072", {"start": v(83.83, -70.16) * mm, "end": v(87.19, -70.99) * mm});
            skLineSegment(sketch, "E1073", {"start": v(87.19, -70.99) * mm, "end": v(89.06, -69.24) * mm});
            skLineSegment(sketch, "E1074", {"start": v(83.77, -69.63) * mm, "end": v(86.82, -68.01) * mm});
            skLineSegment(sketch, "E1075", {"start": v(86.82, -68.01) * mm, "end": v(89.06, -69.24) * mm});
            skLineSegment(sketch, "E1076", {"start": v(84.24, -64.1) * mm, "end": v(85.32, -66.41) * mm});
            skLineSegment(sketch, "E1077", {"start": v(85.32, -66.41) * mm, "end": v(83.5, -69.35) * mm});
            skLineSegment(sketch, "E1078", {"start": v(82.97, -69.25) * mm, "end": v(82.37, -65.84) * mm});
            skLineSegment(sketch, "E1079", {"start": v(82.37, -65.84) * mm, "end": v(84.24, -64.1) * mm});
            skArc(sketch, "E1080", {"start": v(82.78, -70.66) * mm, "mid": v(82.96, -70.72) * mm, "end": v(83.16, -70.73) * mm});
            skArc(sketch, "E1081.trimOffspring", {"start": v(82.36, -69.88) * mm, "mid": v(82.36, -70.08) * mm, "end": v(82.41, -70.27) * mm});
            skArc(sketch, "E1082.trimOffspring", {"start": v(82.97, -69.25) * mm, "mid": v(82.79, -69.3) * mm, "end": v(82.62, -69.41) * mm});
            skArc(sketch, "E1083.trimOffspring", {"start": v(83.77, -69.63) * mm, "mid": v(83.65, -69.47) * mm, "end": v(83.5, -69.35) * mm});
            skArc(sketch, "E1084.trimOffspring", {"start": v(83.64, -70.5) * mm, "mid": v(83.76, -70.35) * mm, "end": v(83.83, -70.16) * mm});
            skLineSegment(sketch, "E1085", {"start": v(79.06, -67.75) * mm, "end": v(79.43, -68.52) * mm});
            skLineSegment(sketch, "E1086", {"start": v(79.43, -68.52) * mm, "end": v(80.81, -68.72) * mm});
            skLineSegment(sketch, "E1087", {"start": v(80.81, -68.72) * mm, "end": v(79.9, -67.65) * mm});
            skLineSegment(sketch, "E1088", {"start": v(79.9, -67.65) * mm, "end": v(79.06, -67.75) * mm});
            skLineSegment(sketch, "E1089", {"start": v(83.98, -65.45) * mm, "end": v(84.34, -66.22) * mm});
            skLineSegment(sketch, "E1090", {"start": v(84.34, -66.22) * mm, "end": v(83.6, -67.41) * mm});
            skLineSegment(sketch, "E1091", {"start": v(83.6, -67.41) * mm, "end": v(83.36, -66.03) * mm});
            skLineSegment(sketch, "E1092", {"start": v(83.36, -66.03) * mm, "end": v(83.98, -65.45) * mm});
            skLineSegment(sketch, "E1093", {"start": v(85.06, -74.17) * mm, "end": v(85.22, -73.33) * mm});
            skLineSegment(sketch, "E1094", {"start": v(85.22, -73.33) * mm, "end": v(84.21, -72.36) * mm});
            skLineSegment(sketch, "E1095", {"start": v(84.21, -72.36) * mm, "end": v(84.32, -73.75) * mm});
            skLineSegment(sketch, "E1096", {"start": v(84.32, -73.75) * mm, "end": v(85.06, -74.17) * mm});
            skLineSegment(sketch, "E1097", {"start": v(87.69, -69.41) * mm, "end": v(86.94, -69) * mm});
            skLineSegment(sketch, "E1098", {"start": v(86.94, -69) * mm, "end": v(85.7, -69.66) * mm});
            skLineSegment(sketch, "E1099", {"start": v(85.7, -69.66) * mm, "end": v(87.06, -70) * mm});
            skLineSegment(sketch, "E1100", {"start": v(87.06, -70) * mm, "end": v(87.69, -69.41) * mm});
            skLineSegment(sketch, "E1101", {"start": v(79.73, -73.14) * mm, "end": v(80.58, -73.03) * mm});
            skLineSegment(sketch, "E1102", {"start": v(80.58, -73.03) * mm, "end": v(81.2, -71.77) * mm});
            skLineSegment(sketch, "E1103", {"start": v(81.2, -71.77) * mm, "end": v(79.9, -72.3) * mm});
            skLineSegment(sketch, "E1104", {"start": v(79.9, -72.3) * mm, "end": v(79.73, -73.14) * mm});
            skLineSegment(sketch, "E1105", {"start": v(-84.66, -67.48) * mm, "end": v(-83, -69.43) * mm});
            skLineSegment(sketch, "E1106", {"start": v(-83, -69.43) * mm, "end": v(-79.58, -69) * mm});
            skLineSegment(sketch, "E1107", {"start": v(-79.45, -68.5) * mm, "end": v(-82.28, -66.52) * mm});
            skLineSegment(sketch, "E1108", {"start": v(-82.28, -66.52) * mm, "end": v(-84.66, -67.48) * mm});
            skLineSegment(sketch, "E1109", {"start": v(-82, -74.01) * mm, "end": v(-79.63, -73.04) * mm});
            skLineSegment(sketch, "E1110", {"start": v(-79.63, -73.04) * mm, "end": v(-78.98, -69.65) * mm});
            skLineSegment(sketch, "E1111", {"start": v(-79.43, -69.37) * mm, "end": v(-82.18, -71.46) * mm});
            skLineSegment(sketch, "E1112", {"start": v(-82.18, -71.46) * mm, "end": v(-82, -74.01) * mm});
            skLineSegment(sketch, "E1113", {"start": v(-74.97, -73.5) * mm, "end": v(-75.16, -70.96) * mm});
            skLineSegment(sketch, "E1114", {"start": v(-75.16, -70.96) * mm, "end": v(-78.18, -69.28) * mm});
            skLineSegment(sketch, "E1115", {"start": v(-78.59, -69.63) * mm, "end": v(-77.45, -72.89) * mm});
            skLineSegment(sketch, "E1116", {"start": v(-77.45, -72.89) * mm, "end": v(-74.97, -73.5) * mm});
            skLineSegment(sketch, "E1117", {"start": v(-78.08, -68.9) * mm, "end": v(-74.63, -68.83) * mm});
            skLineSegment(sketch, "E1118", {"start": v(-74.63, -68.83) * mm, "end": v(-73.27, -66.66) * mm});
            skLineSegment(sketch, "E1119", {"start": v(-78.28, -68.4) * mm, "end": v(-75.76, -66.05) * mm});
            skLineSegment(sketch, "E1120", {"start": v(-75.76, -66.05) * mm, "end": v(-73.27, -66.66) * mm});
            skLineSegment(sketch, "E1121", {"start": v(-79.26, -62.93) * mm, "end": v(-77.62, -64.9) * mm});
            skLineSegment(sketch, "E1122", {"start": v(-77.62, -64.9) * mm, "end": v(-78.62, -68.2) * mm});
            skLineSegment(sketch, "E1123", {"start": v(-79.15, -68.24) * mm, "end": v(-80.6, -65.1) * mm});
            skLineSegment(sketch, "E1124", {"start": v(-80.6, -65.1) * mm, "end": v(-79.26, -62.93) * mm});
            skArc(sketch, "E1125", {"start": v(-78.98, -69.65) * mm, "mid": v(-78.78, -69.67) * mm, "end": v(-78.59, -69.63) * mm});
            skArc(sketch, "E1126.trimOffspring", {"start": v(-79.58, -69) * mm, "mid": v(-79.53, -69.2) * mm, "end": v(-79.43, -69.37) * mm});
            skArc(sketch, "E1127.trimOffspring", {"start": v(-79.15, -68.24) * mm, "mid": v(-79.32, -68.34) * mm, "end": v(-79.45, -68.5) * mm});
            skArc(sketch, "E1128.trimOffspring", {"start": v(-78.28, -68.4) * mm, "mid": v(-78.44, -68.28) * mm, "end": v(-78.62, -68.2) * mm});
            skArc(sketch, "E1129.trimOffspring", {"start": v(-78.18, -69.28) * mm, "mid": v(-78.1, -69.1) * mm, "end": v(-78.08, -68.9) * mm});
            skLineSegment(sketch, "E1130", {"start": v(-83.32, -67.8) * mm, "end": v(-82.76, -68.46) * mm});
            skLineSegment(sketch, "E1131", {"start": v(-82.76, -68.46) * mm, "end": v(-81.37, -68.29) * mm});
            skLineSegment(sketch, "E1132", {"start": v(-81.37, -68.29) * mm, "end": v(-82.52, -67.49) * mm});
            skLineSegment(sketch, "E1133", {"start": v(-82.52, -67.49) * mm, "end": v(-83.32, -67.8) * mm});
            skLineSegment(sketch, "E1134", {"start": v(-79.16, -64.31) * mm, "end": v(-78.61, -64.97) * mm});
            skLineSegment(sketch, "E1135", {"start": v(-78.61, -64.97) * mm, "end": v(-79.02, -66.3) * mm});
            skLineSegment(sketch, "E1136", {"start": v(-79.02, -66.3) * mm, "end": v(-79.61, -65.04) * mm});
            skLineSegment(sketch, "E1137", {"start": v(-79.61, -65.04) * mm, "end": v(-79.16, -64.31) * mm});
            skLineSegment(sketch, "E1138", {"start": v(-75.86, -72.45) * mm, "end": v(-75.92, -71.6) * mm});
            skLineSegment(sketch, "E1139", {"start": v(-75.92, -71.6) * mm, "end": v(-77.15, -70.92) * mm});
            skLineSegment(sketch, "E1140", {"start": v(-77.15, -70.92) * mm, "end": v(-76.69, -72.24) * mm});
            skLineSegment(sketch, "E1141", {"start": v(-76.69, -72.24) * mm, "end": v(-75.86, -72.45) * mm});
            skLineSegment(sketch, "E1142", {"start": v(-74.55, -67.18) * mm, "end": v(-75.38, -66.98) * mm});
            skLineSegment(sketch, "E1143", {"start": v(-75.38, -66.98) * mm, "end": v(-76.4, -67.93) * mm});
            skLineSegment(sketch, "E1144", {"start": v(-76.4, -67.93) * mm, "end": v(-75, -67.9) * mm});
            skLineSegment(sketch, "E1145", {"start": v(-75, -67.9) * mm, "end": v(-74.55, -67.18) * mm});
            skLineSegment(sketch, "E1146", {"start": v(-81.27, -72.84) * mm, "end": v(-80.48, -72.52) * mm});
            skLineSegment(sketch, "E1147", {"start": v(-80.48, -72.52) * mm, "end": v(-80.22, -71.14) * mm});
            skLineSegment(sketch, "E1148", {"start": v(-80.22, -71.14) * mm, "end": v(-81.33, -71.99) * mm});
            skLineSegment(sketch, "E1149", {"start": v(-81.33, -71.99) * mm, "end": v(-81.27, -72.84) * mm});
            skLineSegment(sketch, "E1150", {"start": v(-91.6, -56.35) * mm, "end": v(-93.23, -58.32) * mm});
            skLineSegment(sketch, "E1151", {"start": v(-93.23, -58.32) * mm, "end": v(-92.22, -61.62) * mm});
            skLineSegment(sketch, "E1152", {"start": v(-91.69, -61.66) * mm, "end": v(-90.24, -58.53) * mm});
            skLineSegment(sketch, "E1153", {"start": v(-90.24, -58.53) * mm, "end": v(-91.6, -56.35) * mm});
            skLineSegment(sketch, "E1154", {"start": v(-97.57, -60.1) * mm, "end": v(-96.2, -62.27) * mm});
            skLineSegment(sketch, "E1155", {"start": v(-96.2, -62.27) * mm, "end": v(-92.75, -62.33) * mm});
            skLineSegment(sketch, "E1156", {"start": v(-92.55, -61.83) * mm, "end": v(-95.09, -59.48) * mm});
            skLineSegment(sketch, "E1157", {"start": v(-95.09, -59.48) * mm, "end": v(-97.57, -60.1) * mm});
            skLineSegment(sketch, "E1158", {"start": v(-95.85, -66.94) * mm, "end": v(-93.37, -66.32) * mm});
            skLineSegment(sketch, "E1159", {"start": v(-93.37, -66.32) * mm, "end": v(-92.25, -63.05) * mm});
            skLineSegment(sketch, "E1160", {"start": v(-92.66, -62.7) * mm, "end": v(-95.67, -64.4) * mm});
            skLineSegment(sketch, "E1161", {"start": v(-95.67, -64.4) * mm, "end": v(-95.85, -66.94) * mm});
            skLineSegment(sketch, "E1162", {"start": v(-91.86, -63.08) * mm, "end": v(-91.19, -66.46) * mm});
            skLineSegment(sketch, "E1163", {"start": v(-91.19, -66.46) * mm, "end": v(-88.82, -67.42) * mm});
            skLineSegment(sketch, "E1164", {"start": v(-91.4, -62.8) * mm, "end": v(-88.65, -64.87) * mm});
            skLineSegment(sketch, "E1165", {"start": v(-88.65, -64.87) * mm, "end": v(-88.82, -67.42) * mm});
            skLineSegment(sketch, "E1166", {"start": v(-86.18, -60.88) * mm, "end": v(-87.83, -62.84) * mm});
            skLineSegment(sketch, "E1167", {"start": v(-87.83, -62.84) * mm, "end": v(-91.26, -62.43) * mm});
            skLineSegment(sketch, "E1168", {"start": v(-91.39, -61.91) * mm, "end": v(-88.56, -59.93) * mm});
            skLineSegment(sketch, "E1169", {"start": v(-88.56, -59.93) * mm, "end": v(-86.18, -60.88) * mm});
            skArc(sketch, "E1170", {"start": v(-92.75, -62.33) * mm, "mid": v(-92.73, -62.52) * mm, "end": v(-92.66, -62.7) * mm});
            skArc(sketch, "E1171.trimOffspring", {"start": v(-92.22, -61.62) * mm, "mid": v(-92.4, -61.7) * mm, "end": v(-92.55, -61.83) * mm});
            skArc(sketch, "E1172.trimOffspring", {"start": v(-91.39, -61.91) * mm, "mid": v(-91.52, -61.77) * mm, "end": v(-91.69, -61.66) * mm});
            skArc(sketch, "E1173.trimOffspring", {"start": v(-91.4, -62.8) * mm, "mid": v(-91.3, -62.62) * mm, "end": v(-91.26, -62.43) * mm});
            skArc(sketch, "E1174.trimOffspring", {"start": v(-92.25, -63.05) * mm, "mid": v(-92.06, -63.09) * mm, "end": v(-91.86, -63.08) * mm});
            skLineSegment(sketch, "E1175", {"start": v(-91.69, -57.73) * mm, "end": v(-92.24, -58.39) * mm});
            skLineSegment(sketch, "E1176", {"start": v(-92.24, -58.39) * mm, "end": v(-91.83, -59.73) * mm});
            skLineSegment(sketch, "E1177", {"start": v(-91.83, -59.73) * mm, "end": v(-91.24, -58.46) * mm});
            skLineSegment(sketch, "E1178", {"start": v(-91.24, -58.46) * mm, "end": v(-91.69, -57.73) * mm});
            skLineSegment(sketch, "E1179", {"start": v(-87.53, -61.22) * mm, "end": v(-88.07, -61.87) * mm});
            skLineSegment(sketch, "E1180", {"start": v(-88.07, -61.87) * mm, "end": v(-89.47, -61.7) * mm});
            skLineSegment(sketch, "E1181", {"start": v(-89.47, -61.7) * mm, "end": v(-88.32, -60.9) * mm});
            skLineSegment(sketch, "E1182", {"start": v(-88.32, -60.9) * mm, "end": v(-87.53, -61.22) * mm});
            skLineSegment(sketch, "E1183", {"start": v(-94.97, -65.88) * mm, "end": v(-94.14, -65.67) * mm});
            skLineSegment(sketch, "E1184", {"start": v(-94.14, -65.67) * mm, "end": v(-93.68, -64.35) * mm});
            skLineSegment(sketch, "E1185", {"start": v(-93.68, -64.35) * mm, "end": v(-94.9, -65.03) * mm});
            skLineSegment(sketch, "E1186", {"start": v(-94.9, -65.03) * mm, "end": v(-94.97, -65.88) * mm});
            skLineSegment(sketch, "E1187", {"start": v(-89.55, -66.25) * mm, "end": v(-89.5, -65.4) * mm});
            skLineSegment(sketch, "E1188", {"start": v(-89.5, -65.4) * mm, "end": v(-90.61, -64.56) * mm});
            skLineSegment(sketch, "E1189", {"start": v(-90.61, -64.56) * mm, "end": v(-90.34, -65.93) * mm});
            skLineSegment(sketch, "E1190", {"start": v(-90.34, -65.93) * mm, "end": v(-89.55, -66.25) * mm});
            skLineSegment(sketch, "E1191", {"start": v(-96.29, -60.62) * mm, "end": v(-95.83, -61.34) * mm});
            skLineSegment(sketch, "E1192", {"start": v(-95.83, -61.34) * mm, "end": v(-94.43, -61.36) * mm});
            skLineSegment(sketch, "E1193", {"start": v(-94.43, -61.36) * mm, "end": v(-95.46, -60.41) * mm});
            skLineSegment(sketch, "E1194", {"start": v(-95.46, -60.41) * mm, "end": v(-96.29, -60.62) * mm});
            skSolve(sketch);
        }
        {
            var Q0;
            Q0=qCreatedBy(makeId("Right.planeOp"),FACE);
            var sketch = newSketch(context, id + "F3", { "sketchPlane" : qUnion([Q0])});
            skLineSegment(sketch, "E1195", {"start": v(0, -70.92) * mm, "end": v(0, 69.35) * mm, "construction": true});
            skSolve(sketch);
        }
        {
            var Q0;
            Q0=makeQuery(id+"F1.opExtrude","CAP_FACE",FACE,{"disambiguationData":[OSD([sQuery(id+"F0.wireOp",EDGE,"E0.bottom"),sQuery(id+"F0.wireOp",EDGE,"E0.top"),sQuery(id+"F0.wireOp",EDGE,"E0.left"),sQuery(id+"F0.wireOp",EDGE,"E0.right"),sQuery(id+"F0.wireOp",EDGE,"kvcqsOdL-v7G7-uprB-0sNa-MCxYedLtEpX4"),sQuery(id+"F0.wireOp",EDGE,"FiKvVNeF-WQ3T-xo78-YCTY-fOMMCtKvFc36"),sQuery(id+"F0.wireOp",EDGE,"E12"),sQuery(id+"F0.wireOp",EDGE,"E11.MirrorCS"),sQuery(id+"F0.wireOp",EDGE,"c8cf1958-df2a-43db-8a51-ccb89cce498c1.MirrorCS"),sQuery(id+"F0.wireOp",EDGE,"b5f25a3e-5a5b-413b-84b4-cc5ad052e2f90.MirrorCS"),sQuery(id+"F0.wireOp",EDGE,"E13.MirrorCS"),sQuery(id+"F0.wireOp",EDGE,"bd7b76a7-2dc2-4ffb-bbfe-847ced00b9070.MirrorCS"),sQuery(id+"F0.wireOp",EDGE,"E1.trimOffspring"),sQuery(id+"F0.wireOp",EDGE,"E2.trimOffspring"),sQuery(id+"F0.wireOp",EDGE,"E3.trimOffspring"),sQuery(id+"F0.wireOp",EDGE,"E4.trimOffspring")])],"isStart":false});
            var sketch = newSketch(context, id + "F4", { "sketchPlane" : qUnion([Q0])});
            skLineSegment(sketch, "E1196.bottom", {"start": v(-76.2, 50.8) * mm, "end": v(76.2, 50.8) * mm});
            skLineSegment(sketch, "E1196.top", {"start": v(-76.2, -50.8) * mm, "end": v(76.2, -50.8) * mm});
            skLineSegment(sketch, "E1196.left", {"start": v(-76.2, 50.8) * mm, "end": v(-76.2, -50.8) * mm});
            skLineSegment(sketch, "E1196.right", {"start": v(76.2, 50.8) * mm, "end": v(76.2, -50.8) * mm});
            skSolve(sketch);
        }
        {
            var Q0;
            Q0=makeQuery(id+"F4.imprint","IMPRINT",FACE,{"disambiguationData":[TD([[makeQuery(id+"F4.imprint","IMPRINT",EDGE,{"derivedFrom":sQuery(id+"F4.wireOp",EDGE,"E1196.bottom")}),-1.0]])]});
            extrude(context, id + "F5", {"entities" : qUnion([Q0]), "operationType" : NewBodyOperationType.REMOVE, "endBound" : BoundingType.THROUGH_ALL, "oppositeDirection" : true, "depth" : 5 * mm});
        }
        {
            var Q0;
            Q0=qSketchRegion(id+"F2",true);
            extrude(context, id + "F6", {"entities" : qUnion([Q0]), "operationType" : NewBodyOperationType.ADD, "depth" : 2 * mm});
        }
        {
            var Q0;
            {var subQ0=sQuery(id+"F0.wireOp",EDGE,"E12");var subQ1=sQuery(id+"F0.wireOp",EDGE,"E0.bottom");var subQ2=sQuery(id+"F0.wireOp",EDGE,"b5f25a3e-5a5b-413b-84b4-cc5ad052e2f90.MirrorCS");var subQ3=sQuery(id+"F0.wireOp",EDGE,"E13.MirrorCS");var subQ4=sQuery(id+"F0.wireOp",EDGE,"bd7b76a7-2dc2-4ffb-bbfe-847ced00b9070.MirrorCS");var subQ5=sQuery(id+"F0.wireOp",EDGE,"E1.trimOffspring");var subQ6=sQuery(id+"F0.wireOp",EDGE,"E2.trimOffspring");var subQ7=sQuery(id+"F0.wireOp",EDGE,"E3.trimOffspring");var subQ8=sQuery(id+"F0.wireOp",EDGE,"E4.trimOffspring");var subQ9=sQuery(id+"F0.wireOp",EDGE,"E0.top");var subQ10=sQuery(id+"F0.wireOp",EDGE,"E0.left");var subQ11=sQuery(id+"F0.wireOp",EDGE,"E0.right");var subQ12=sQuery(id+"F0.wireOp",EDGE,"kvcqsOdL-v7G7-uprB-0sNa-MCxYedLtEpX4");var subQ13=sQuery(id+"F0.wireOp",EDGE,"FiKvVNeF-WQ3T-xo78-YCTY-fOMMCtKvFc36");var subQ14=sQuery(id+"F0.wireOp",EDGE,"E11.MirrorCS");var subQ15=sQuery(id+"F0.wireOp",EDGE,"c8cf1958-df2a-43db-8a51-ccb89cce498c1.MirrorCS");Q0=makeQuery(id+"F6.boolean.opBoolean","SPLIT",FACE,{"disambiguationData":[TD([makeQuery(id+"F1.opExtrude","SWEPT_FACE",FACE,{"disambiguationData":[OSD([subQ1])]})])],"derivedFrom":makeQuery(id+"F1.opExtrude","CAP_FACE",FACE,{"disambiguationData":[OSD([subQ1,subQ9,subQ10,subQ11,subQ12,subQ13,subQ0,subQ14,subQ15,subQ2,subQ3,subQ4,subQ5,subQ6,subQ7,subQ8])],"isStart":false})});}
            var sketch = newSketch(context, id + "F7", { "sketchPlane" : qUnion([Q0])});
            skText(sketch, "E1197", { "text": "          I LOVE YOU GG!\nMY FIRST CHRISTMAS - 2016", "fontName": "OpenSans-BoldItalic.ttf"});
            const initialGuessF7  = {"E1197": [-0.08416, 0.04974, 0, -1, 0.00528]};
            skSetInitialGuess(sketch, initialGuessF7);
            skSolve(sketch);
        }
        {
            var Q0;
            Q0=qSketchRegion(id+"F7",true);
            extrude(context, id + "F8", {"entities" : qUnion([Q0]), "operationType" : NewBodyOperationType.ADD, "depth" : 2 * mm});
        }
        {
            var Q0;
            {var subQ240=sQuery(id+"F0.wireOp",EDGE,"c8cf1958-df2a-43db-8a51-ccb89cce498c1.MirrorCS");var subQ244=sQuery(id+"F0.wireOp",EDGE,"E11.MirrorCS");var subQ248=sQuery(id+"F0.wireOp",EDGE,"FiKvVNeF-WQ3T-xo78-YCTY-fOMMCtKvFc36");var subQ251=sQuery(id+"F0.wireOp",EDGE,"kvcqsOdL-v7G7-uprB-0sNa-MCxYedLtEpX4");var subQ254=sQuery(id+"F0.wireOp",EDGE,"E0.right");var subQ257=sQuery(id+"F0.wireOp",EDGE,"E0.left");var subQ260=sQuery(id+"F0.wireOp",EDGE,"E0.top");var subQ313=sQuery(id+"F0.wireOp",EDGE,"E4.trimOffspring");var subQ320=sQuery(id+"F0.wireOp",EDGE,"E3.trimOffspring");var subQ330=sQuery(id+"F0.wireOp",EDGE,"E2.trimOffspring");var subQ338=sQuery(id+"F0.wireOp",EDGE,"E1.trimOffspring");var subQ346=sQuery(id+"F0.wireOp",EDGE,"bd7b76a7-2dc2-4ffb-bbfe-847ced00b9070.MirrorCS");var subQ354=sQuery(id+"F0.wireOp",EDGE,"E13.MirrorCS");var subQ362=sQuery(id+"F0.wireOp",EDGE,"b5f25a3e-5a5b-413b-84b4-cc5ad052e2f90.MirrorCS");var subQ383=sQuery(id+"F0.wireOp",EDGE,"E0.bottom");var subQ384=makeQuery(id+"F1.opExtrude","SWEPT_FACE",FACE,{"disambiguationData":[OSD([subQ383])]});var subQ406=sQuery(id+"F0.wireOp",EDGE,"E12");Q0=makeQuery(id+"F8.boolean.opBoolean","SPLIT",FACE,{"disambiguationData":[TD([subQ384])],"derivedFrom":makeQuery(id+"F6.boolean.opBoolean","SPLIT",FACE,{"disambiguationData":[TD([subQ384])],"derivedFrom":makeQuery(id+"F1.opExtrude","CAP_FACE",FACE,{"disambiguationData":[OSD([subQ383,subQ260,subQ257,subQ254,subQ251,subQ248,subQ406,subQ244,subQ240,subQ362,subQ354,subQ346,subQ338,subQ330,subQ320,subQ313])],"isStart":false})})});}
            var sketch = newSketch(context, id + "F9", { "sketchPlane" : qUnion([Q0])});
            skLineSegment(sketch, "E1198.0", {"start": v(34.4, 50.8) * mm, "end": v(76.2, 50.8) * mm});
            skLineSegment(sketch, "E1199.0", {"start": v(76.2, 50.8) * mm, "end": v(76.2, 15.09) * mm});
            skLineSegment(sketch, "E1200.bottom", {"start": v(76.2, 50.8) * mm, "end": v(-76.2, 50.8) * mm});
            skLineSegment(sketch, "E1200.top", {"start": v(76.2, -50.8) * mm, "end": v(-76.2, -50.8) * mm});
            skLineSegment(sketch, "E1200.left", {"start": v(76.2, 50.8) * mm, "end": v(76.2, -50.8) * mm});
            skLineSegment(sketch, "E1200.right", {"start": v(-76.2, 50.8) * mm, "end": v(-76.2, -50.8) * mm});
            skPoint(sketch, "E1200.middle", {"position": v(0, 0) * mm});
            skLineSegment(sketch, "E1201.bottom", {"start": v(73.2, 47.8) * mm, "end": v(-73.2, 47.8) * mm});
            skLineSegment(sketch, "E1201.top", {"start": v(73.2, -47.8) * mm, "end": v(-73.2, -47.8) * mm});
            skLineSegment(sketch, "E1201.left", {"start": v(73.2, 47.8) * mm, "end": v(73.2, -47.8) * mm});
            skLineSegment(sketch, "E1201.right", {"start": v(-73.2, 47.8) * mm, "end": v(-73.2, -47.8) * mm});
            skSolve(sketch);
        }
        {
            var Q0;
            Q0=qSketchRegion(id+"F9",true);
            extrude(context, id + "F10", {"entities" : qUnion([Q0]), "operationType" : NewBodyOperationType.ADD, "oppositeDirection" : true, "depth" : 2 * mm});
        }
        {
            var Q0;
            Q0=qCreatedBy(makeId("Top.planeOp"),FACE);
            var sketch = newSketch(context, id + "F11", { "sketchPlane" : qUnion([Q0])});
            skLineSegment(sketch, "E1202", {"start": v(-57.24, -90.27) * mm, "end": v(-57.24, -27.65) * mm});
            skLineSegment(sketch, "E1203", {"start": v(-57.24, -27.65) * mm, "end": v(-116.23, -27.65) * mm});
            skLineSegment(sketch, "E1204", {"start": v(-57.24, -90.27) * mm, "end": v(106.8, -90.27) * mm});
            skLineSegment(sketch, "E1205", {"start": v(106.8, -90.27) * mm, "end": v(106.8, 89.16) * mm});
            skLineSegment(sketch, "E1206", {"start": v(106.8, 89.16) * mm, "end": v(-116.23, 89.16) * mm});
            skLineSegment(sketch, "E1207", {"start": v(-116.23, 89.16) * mm, "end": v(-116.23, -27.65) * mm});
            skSolve(sketch);
        }
        {
            var Q0;
            Q0 = qSketchRegion(id + "F11", true);
            extrude(context, id + "F12", {"entities" : qUnion([Q0]), "operationType" : NewBodyOperationType.REMOVE, "endBound" : BoundingType.SYMMETRIC, "oppositeDirection" : true, "depth" : 25 * mm});
        }
    });
